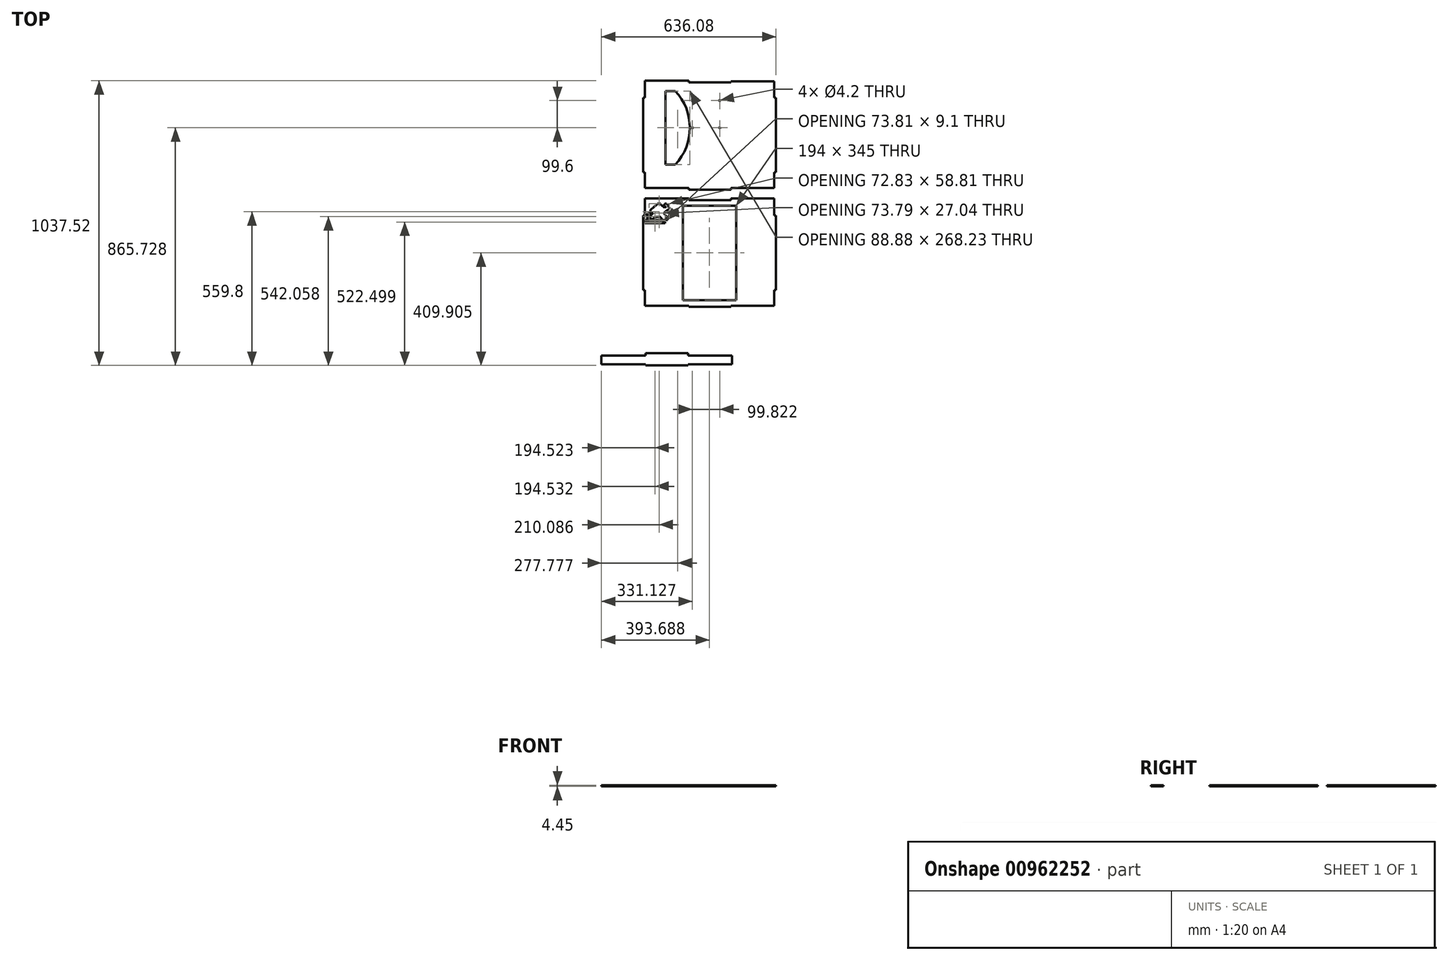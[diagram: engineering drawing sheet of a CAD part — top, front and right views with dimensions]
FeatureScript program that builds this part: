
annotation { "Feature Type Name" : "Feature", "Feature Type Description" : "" }
export const myFeature = defineFeature(function(context is Context, id is Id, definition is map)
    precondition{}
    {
        {
            var Q0;
            Q0=qCreatedBy(makeId("Top.planeOp"),FACE);
            var sketch = newSketch(context, id + "F0", { "sketchPlane" : qUnion([Q0])});
            skLineSegment(sketch, "E0.bottom", {"start": v(279.74, -310.31) * mm, "end": v(85.74, -310.31) * mm});
            skLineSegment(sketch, "E0.top", {"start": v(279.74, 34.69) * mm, "end": v(85.74, 34.69) * mm});
            skLineSegment(sketch, "E0.left", {"start": v(279.74, -310.31) * mm, "end": v(279.74, 34.69) * mm});
            skLineSegment(sketch, "E0.right", {"start": v(85.74, -310.31) * mm, "end": v(85.74, 34.69) * mm});
            skPoint(sketch, "E0.middle", {"position": v(182.74, -137.81) * mm});
            skLineSegment(sketch, "E1.bottom", {"start": v(418.8, -329.81) * mm, "end": v(260.26, -329.81) * mm});
            skLineSegment(sketch, "E1.top", {"start": v(260.26, 54.19) * mm, "end": v(107.1, 54.19) * mm});
            skLineSegment(sketch, "E1.left", {"start": v(418.8, -329.81) * mm, "end": v(418.8, -273.57) * mm});
            skLineSegment(sketch, "E1.right", {"start": v(-53.32, -329.81) * mm, "end": v(-53.32, -273.57) * mm});
            skLineSegment(sketch, "E2.top", {"start": v(-53.32, 60.52) * mm, "end": v(107.1, 60.52) * mm});
            skLineSegment(sketch, "E2.left", {"start": v(-53.32, 54.19) * mm, "end": v(-53.32, 60.52) * mm});
            skLineSegment(sketch, "E2.right", {"start": v(107.1, 54.19) * mm, "end": v(107.1, 60.52) * mm});
            skLineSegment(sketch, "E3.MirrorCS", {"start": v(260.26, 54.19) * mm, "end": v(260.26, 60.52) * mm});
            skLineSegment(sketch, "E4.top", {"start": v(107.1, -334.26) * mm, "end": v(260.26, -334.26) * mm});
            skLineSegment(sketch, "E4.left", {"start": v(107.1, -329.81) * mm, "end": v(107.1, -334.26) * mm});
            skLineSegment(sketch, "E4.right", {"start": v(260.26, -329.81) * mm, "end": v(260.26, -334.26) * mm});
            skLineSegment(sketch, "E5.trimOffspring", {"start": v(107.1, -329.81) * mm, "end": v(-53.32, -329.81) * mm});
            skLineSegment(sketch, "E6.bottom", {"start": v(425.13, -273.57) * mm, "end": v(418.8, -273.57) * mm});
            skLineSegment(sketch, "E6.top", {"start": v(425.13, -2.06) * mm, "end": v(418.8, -2.06) * mm});
            skLineSegment(sketch, "E6.left", {"start": v(425.13, -273.57) * mm, "end": v(425.13, -2.06) * mm});
            skLineSegment(sketch, "E6.right", {"start": v(-59.65, -273.57) * mm, "end": v(-59.65, -2.06) * mm});
            skLineSegment(sketch, "E7.trimOffspring", {"start": v(-53.32, -2.06) * mm, "end": v(-59.65, -2.06) * mm});
            skLineSegment(sketch, "E8.trimOffspring", {"start": v(-53.32, -273.57) * mm, "end": v(-59.65, -273.57) * mm});
            skLineSegment(sketch, "E9.trimOffspring", {"start": v(-53.32, -2.06) * mm, "end": v(-53.32, 54.19) * mm});
            skLineSegment(sketch, "E10.trimOffspring", {"start": v(418.8, -2.06) * mm, "end": v(418.8, 54.19) * mm});
            skLineSegment(sketch, "E11", {"start": v(-50.59, -20.7) * mm, "end": v(-50.59, -22.21) * mm});
            skLineSegment(sketch, "E12", {"start": v(-50.59, -22.21) * mm, "end": v(-49.15, -22.21) * mm});
            skLineSegment(sketch, "E13", {"start": v(-49.15, -22.21) * mm, "end": v(-49.15, -23.7) * mm});
            skLineSegment(sketch, "E14", {"start": v(-49.15, -23.7) * mm, "end": v(-47.72, -23.7) * mm});
            skLineSegment(sketch, "E15", {"start": v(-47.72, -23.7) * mm, "end": v(-47.72, -25.08) * mm});
            skLineSegment(sketch, "E16", {"start": v(-47.72, -25.08) * mm, "end": v(-46.45, -25.08) * mm});
            skLineSegment(sketch, "E17", {"start": v(-46.45, -25.08) * mm, "end": v(-46.45, -23.64) * mm});
            skLineSegment(sketch, "E18", {"start": v(-46.45, -23.64) * mm, "end": v(-44.99, -23.64) * mm});
            skLineSegment(sketch, "E19", {"start": v(-44.99, -23.64) * mm, "end": v(-44.99, -22.1) * mm});
            skLineSegment(sketch, "E20", {"start": v(-44.99, -22.1) * mm, "end": v(-43.53, -22.1) * mm});
            skLineSegment(sketch, "E21", {"start": v(-43.53, -22.1) * mm, "end": v(-43.53, -20.7) * mm});
            skLineSegment(sketch, "E22", {"start": v(-43.53, -20.7) * mm, "end": v(-39.25, -20.7) * mm});
            skLineSegment(sketch, "E23", {"start": v(-39.25, -20.7) * mm, "end": v(-39.25, -22.1) * mm});
            skLineSegment(sketch, "E24", {"start": v(-39.25, -22.1) * mm, "end": v(-37.82, -22.1) * mm});
            skLineSegment(sketch, "E25", {"start": v(-37.82, -22.1) * mm, "end": v(-37.82, -23.75) * mm});
            skLineSegment(sketch, "E26", {"start": v(-37.82, -23.75) * mm, "end": v(-36.36, -23.75) * mm});
            skLineSegment(sketch, "E27", {"start": v(-36.36, -23.75) * mm, "end": v(-36.36, -25.1) * mm});
            skLineSegment(sketch, "E28", {"start": v(-36.36, -25.1) * mm, "end": v(-35, -25.1) * mm});
            skLineSegment(sketch, "E29", {"start": v(-35, -25.1) * mm, "end": v(-35, -23.75) * mm});
            skLineSegment(sketch, "E30", {"start": v(-35, -23.75) * mm, "end": v(-33.6, -23.75) * mm});
            skLineSegment(sketch, "E31", {"start": v(-33.6, -23.75) * mm, "end": v(-33.6, -22.24) * mm});
            skLineSegment(sketch, "E32", {"start": v(-33.6, -22.24) * mm, "end": v(-32.2, -22.24) * mm});
            skLineSegment(sketch, "E33", {"start": v(-32.2, -22.24) * mm, "end": v(-32.2, -20.67) * mm});
            skLineSegment(sketch, "E34", {"start": v(-32.2, -20.67) * mm, "end": v(-27.9, -20.67) * mm});
            skLineSegment(sketch, "E35", {"start": v(-27.9, -20.67) * mm, "end": v(-27.9, -22.13) * mm});
            skLineSegment(sketch, "E36", {"start": v(-27.9, -22.13) * mm, "end": v(-26.46, -22.13) * mm});
            skLineSegment(sketch, "E37", {"start": v(-26.46, -22.13) * mm, "end": v(-26.46, -23.75) * mm});
            skLineSegment(sketch, "E38", {"start": v(-26.46, -23.75) * mm, "end": v(-25.03, -23.75) * mm});
            skLineSegment(sketch, "E39", {"start": v(-25.03, -23.75) * mm, "end": v(-25.03, -25.1) * mm});
            skLineSegment(sketch, "E40", {"start": v(-25.03, -25.1) * mm, "end": v(-24.14, -25.1) * mm});
            skLineSegment(sketch, "E41", {"start": v(-24.14, -25.1) * mm, "end": v(-24.14, -23.75) * mm});
            skLineSegment(sketch, "E42", {"start": v(-24.14, -23.75) * mm, "end": v(-22.98, -23.75) * mm});
            skLineSegment(sketch, "E43", {"start": v(-22.98, -23.75) * mm, "end": v(-22.98, -22.24) * mm});
            skLineSegment(sketch, "E44", {"start": v(-22.98, -22.24) * mm, "end": v(-21.62, -22.24) * mm});
            skLineSegment(sketch, "E45", {"start": v(-21.62, -22.24) * mm, "end": v(-21.62, -20.7) * mm});
            skLineSegment(sketch, "E46", {"start": v(-50.59, -20.7) * mm, "end": v(-53.32, -20.7) * mm});
            skLineSegment(sketch, "E47", {"start": v(-53.32, -20.7) * mm, "end": v(-53.32, -22.18) * mm});
            skLineSegment(sketch, "E48", {"start": v(-53.32, -22.18) * mm, "end": v(-52.02, -22.18) * mm});
            skLineSegment(sketch, "E49", {"start": v(-52.02, -22.18) * mm, "end": v(-52.02, -23.7) * mm});
            skLineSegment(sketch, "E50", {"start": v(-52.02, -23.7) * mm, "end": v(-50.59, -23.7) * mm});
            skLineSegment(sketch, "E51", {"start": v(-50.59, -23.7) * mm, "end": v(-50.59, -25.21) * mm});
            skLineSegment(sketch, "E52", {"start": v(-50.59, -25.21) * mm, "end": v(-49.18, -25.21) * mm});
            skLineSegment(sketch, "E53", {"start": v(-49.18, -25.21) * mm, "end": v(-49.18, -26.73) * mm});
            skLineSegment(sketch, "E54", {"start": v(-49.18, -26.73) * mm, "end": v(-53.32, -26.73) * mm});
            skLineSegment(sketch, "E55", {"start": v(-53.32, -26.73) * mm, "end": v(-53.32, -28.19) * mm});
            skLineSegment(sketch, "E56", {"start": v(-53.32, -28.19) * mm, "end": v(20.49, -28.19) * mm});
            skLineSegment(sketch, "E57", {"start": v(20.49, -28.19) * mm, "end": v(20.49, -25.14) * mm});
            skLineSegment(sketch, "E58", {"start": v(20.49, -25.14) * mm, "end": v(19.7, -25.14) * mm});
            skLineSegment(sketch, "E59", {"start": v(19.7, -25.14) * mm, "end": v(19.7, -23.73) * mm});
            skLineSegment(sketch, "E60", {"start": v(19.7, -23.73) * mm, "end": v(18.35, -23.73) * mm});
            skLineSegment(sketch, "E61", {"start": v(18.35, -23.73) * mm, "end": v(18.35, -22.21) * mm});
            skLineSegment(sketch, "E62", {"start": v(18.35, -22.21) * mm, "end": v(16.85, -22.21) * mm});
            skLineSegment(sketch, "E63", {"start": v(16.85, -22.21) * mm, "end": v(16.85, -20.7) * mm});
            skLineSegment(sketch, "E64", {"start": v(16.85, -20.7) * mm, "end": v(12.58, -20.7) * mm});
            skLineSegment(sketch, "E65", {"start": v(12.58, -20.7) * mm, "end": v(12.58, -22.21) * mm});
            skLineSegment(sketch, "E66", {"start": v(12.58, -22.21) * mm, "end": v(11.21, -22.21) * mm});
            skLineSegment(sketch, "E67", {"start": v(11.21, -22.21) * mm, "end": v(11.21, -23.76) * mm});
            skLineSegment(sketch, "E68", {"start": v(11.21, -23.76) * mm, "end": v(9.69, -23.76) * mm});
            skLineSegment(sketch, "E69", {"start": v(9.69, -23.76) * mm, "end": v(9.69, -25.14) * mm});
            skLineSegment(sketch, "E70.bottom", {"start": v(-21.62, -20.7) * mm, "end": v(-17.3, -20.7) * mm});
            skLineSegment(sketch, "E70.top", {"start": v(-20.12, -22.19) * mm, "end": v(-18.62, -22.19) * mm});
            skLineSegment(sketch, "E70.left", {"start": v(-21.62, -20.7) * mm, "end": v(-21.62, -22.19) * mm});
            skLineSegment(sketch, "E70.right", {"start": v(-17.3, -20.7) * mm, "end": v(-17.3, -22.19) * mm});
            skLineSegment(sketch, "E71.bottom", {"start": v(-17.3, -22.19) * mm, "end": v(-15.92, -22.19) * mm});
            skLineSegment(sketch, "E71.top", {"start": v(-18.62, -23.77) * mm, "end": v(-17.27, -23.77) * mm});
            skLineSegment(sketch, "E71.left", {"start": v(-18.62, -22.19) * mm, "end": v(-18.62, -23.77) * mm});
            skLineSegment(sketch, "E71.right", {"start": v(-15.92, -22.19) * mm, "end": v(-15.92, -23.77) * mm});
            skLineSegment(sketch, "E72.bottom", {"start": v(-15.92, -23.77) * mm, "end": v(-14.48, -23.77) * mm});
            skLineSegment(sketch, "E72.top", {"start": v(-17.27, -25.08) * mm, "end": v(-15.88, -25.08) * mm});
            skLineSegment(sketch, "E72.left", {"start": v(-17.27, -23.77) * mm, "end": v(-17.27, -25.08) * mm});
            skLineSegment(sketch, "E72.right", {"start": v(-14.48, -23.77) * mm, "end": v(-14.48, -25.08) * mm});
            skLineSegment(sketch, "E73.bottom", {"start": v(-14.48, -25.08) * mm, "end": v(-13.07, -25.08) * mm});
            skLineSegment(sketch, "E73.left", {"start": v(-15.88, -25.08) * mm, "end": v(-15.88, -26.74) * mm});
            skLineSegment(sketch, "E73.right", {"start": v(-11.62, -25.08) * mm, "end": v(-11.62, -26.74) * mm});
            skLineSegment(sketch, "E74.bottom", {"start": v(-13.07, -23.72) * mm, "end": v(-11.62, -23.72) * mm});
            skLineSegment(sketch, "E74.top", {"start": v(-11.62, -25.08) * mm, "end": v(-10.28, -25.08) * mm});
            skLineSegment(sketch, "E74.left", {"start": v(-13.07, -23.72) * mm, "end": v(-13.07, -25.08) * mm});
            skLineSegment(sketch, "E74.right", {"start": v(-10.28, -23.72) * mm, "end": v(-10.28, -25.08) * mm});
            skLineSegment(sketch, "E75.top", {"start": v(-10.28, -23.72) * mm, "end": v(-8.73, -23.72) * mm});
            skLineSegment(sketch, "E75.left", {"start": v(-11.62, -22.23) * mm, "end": v(-11.62, -23.72) * mm});
            skLineSegment(sketch, "E75.right", {"start": v(-8.73, -22.23) * mm, "end": v(-8.73, -23.72) * mm});
            skLineSegment(sketch, "E76.bottom", {"start": v(-10.26, -20.7) * mm, "end": v(-5.89, -20.7) * mm});
            skLineSegment(sketch, "E76.left", {"start": v(-10.26, -20.7) * mm, "end": v(-10.26, -22.23) * mm});
            skLineSegment(sketch, "E76.right", {"start": v(-5.89, -20.7) * mm, "end": v(-5.89, -22.23) * mm});
            skLineSegment(sketch, "E77", {"start": v(-20.12, -22.19) * mm, "end": v(-20.12, -23.66) * mm});
            skLineSegment(sketch, "E78", {"start": v(-20.12, -23.66) * mm, "end": v(-21.6, -23.66) * mm});
            skLineSegment(sketch, "E79", {"start": v(-21.6, -23.66) * mm, "end": v(-21.6, -25.18) * mm});
            skLineSegment(sketch, "E80", {"start": v(-21.6, -25.18) * mm, "end": v(-22.94, -25.18) * mm});
            skLineSegment(sketch, "E81", {"start": v(-22.94, -25.18) * mm, "end": v(-22.94, -26.67) * mm});
            skLineSegment(sketch, "E82", {"start": v(-22.94, -26.67) * mm, "end": v(-15.88, -26.74) * mm});
            skLineSegment(sketch, "E83.bottom", {"start": v(-5.89, -22.23) * mm, "end": v(-4.49, -22.23) * mm});
            skLineSegment(sketch, "E83.top", {"start": v(-7.34, -23.76) * mm, "end": v(-5.91, -23.76) * mm});
            skLineSegment(sketch, "E83.left", {"start": v(-7.34, -22.23) * mm, "end": v(-7.34, -23.76) * mm});
            skLineSegment(sketch, "E83.right", {"start": v(-4.49, -22.23) * mm, "end": v(-4.49, -23.76) * mm});
            skLineSegment(sketch, "E84.bottom", {"start": v(-4.49, -23.76) * mm, "end": v(-3.06, -23.76) * mm});
            skLineSegment(sketch, "E84.top", {"start": v(-5.91, -25.18) * mm, "end": v(-4.49, -25.18) * mm});
            skLineSegment(sketch, "E84.left", {"start": v(-5.91, -23.76) * mm, "end": v(-5.91, -25.18) * mm});
            skLineSegment(sketch, "E84.right", {"start": v(-3.06, -23.76) * mm, "end": v(-3.06, -25.18) * mm});
            skLineSegment(sketch, "E85.bottom", {"start": v(-3.06, -25.18) * mm, "end": v(-1.72, -25.18) * mm});
            skLineSegment(sketch, "E85.left", {"start": v(-4.49, -25.18) * mm, "end": v(-4.49, -26.73) * mm});
            skLineSegment(sketch, "E85.right", {"start": v(-0.26, -25.18) * mm, "end": v(-0.26, -26.73) * mm});
            skLineSegment(sketch, "E86", {"start": v(-11.62, -26.74) * mm, "end": v(-4.49, -26.73) * mm});
            skLineSegment(sketch, "E87", {"start": v(-0.26, -25.18) * mm, "end": v(1.2, -25.18) * mm});
            skLineSegment(sketch, "E88", {"start": v(1.2, -25.18) * mm, "end": v(1.2, -23.77) * mm});
            skLineSegment(sketch, "E89", {"start": v(1.2, -23.77) * mm, "end": v(2.63, -23.77) * mm});
            skLineSegment(sketch, "E90", {"start": v(2.63, -23.77) * mm, "end": v(2.63, -22.25) * mm});
            skLineSegment(sketch, "E91", {"start": v(2.63, -22.25) * mm, "end": v(3.95, -22.25) * mm});
            skLineSegment(sketch, "E92", {"start": v(3.95, -22.25) * mm, "end": v(3.95, -23.77) * mm});
            skLineSegment(sketch, "E93", {"start": v(3.95, -23.77) * mm, "end": v(5.34, -23.77) * mm});
            skLineSegment(sketch, "E94", {"start": v(5.34, -23.77) * mm, "end": v(5.34, -25.18) * mm});
            skLineSegment(sketch, "E95", {"start": v(5.34, -25.18) * mm, "end": v(6.82, -25.18) * mm});
            skLineSegment(sketch, "E96", {"start": v(6.82, -25.18) * mm, "end": v(6.82, -26.73) * mm});
            skLineSegment(sketch, "E97", {"start": v(6.82, -26.73) * mm, "end": v(-0.26, -26.73) * mm});
            skLineSegment(sketch, "E98.right", {"start": v(11.18, -25.18) * mm, "end": v(11.18, -26.73) * mm});
            skLineSegment(sketch, "E99", {"start": v(11.18, -25.18) * mm, "end": v(12.64, -25.18) * mm});
            skLineSegment(sketch, "E100", {"start": v(12.64, -25.18) * mm, "end": v(12.64, -23.77) * mm});
            skLineSegment(sketch, "E101", {"start": v(12.64, -23.77) * mm, "end": v(14.07, -23.77) * mm});
            skLineSegment(sketch, "E102", {"start": v(14.07, -23.77) * mm, "end": v(14.07, -22.25) * mm});
            skLineSegment(sketch, "E103", {"start": v(14.07, -22.25) * mm, "end": v(15.4, -22.25) * mm});
            skLineSegment(sketch, "E104", {"start": v(15.4, -22.25) * mm, "end": v(15.4, -23.77) * mm});
            skLineSegment(sketch, "E105", {"start": v(15.4, -23.77) * mm, "end": v(16.79, -23.77) * mm});
            skLineSegment(sketch, "E106", {"start": v(16.79, -23.77) * mm, "end": v(16.79, -25.18) * mm});
            skLineSegment(sketch, "E107", {"start": v(16.79, -25.18) * mm, "end": v(18.26, -25.18) * mm});
            skLineSegment(sketch, "E108", {"start": v(18.26, -25.18) * mm, "end": v(18.26, -26.73) * mm});
            skLineSegment(sketch, "E109", {"start": v(18.26, -26.73) * mm, "end": v(11.18, -26.73) * mm});
            skLineSegment(sketch, "E110", {"start": v(-1.72, -25.18) * mm, "end": v(-1.72, -23.84) * mm});
            skLineSegment(sketch, "E111", {"start": v(-1.72, -23.84) * mm, "end": v(-1.72, -23.76) * mm});
            skLineSegment(sketch, "E112", {"start": v(-1.72, -23.76) * mm, "end": v(-0.3, -23.76) * mm});
            skLineSegment(sketch, "E113", {"start": v(-0.3, -23.76) * mm, "end": v(-0.3, -22.23) * mm});
            skLineSegment(sketch, "E114", {"start": v(-0.3, -22.23) * mm, "end": v(1.15, -22.23) * mm});
            skLineSegment(sketch, "E115", {"start": v(1.15, -22.23) * mm, "end": v(1.15, -20.69) * mm});
            skLineSegment(sketch, "E116", {"start": v(1.15, -20.69) * mm, "end": v(5.42, -20.69) * mm});
            skLineSegment(sketch, "E117", {"start": v(5.42, -20.69) * mm, "end": v(5.42, -22.13) * mm});
            skLineSegment(sketch, "E118", {"start": v(5.42, -22.13) * mm, "end": v(6.87, -22.13) * mm});
            skLineSegment(sketch, "E119", {"start": v(6.87, -22.13) * mm, "end": v(6.87, -23.76) * mm});
            skLineSegment(sketch, "E120", {"start": v(6.87, -23.76) * mm, "end": v(8.33, -23.76) * mm});
            skLineSegment(sketch, "E121", {"start": v(8.33, -23.76) * mm, "end": v(8.33, -25.14) * mm});
            skLineSegment(sketch, "E122", {"start": v(8.33, -25.14) * mm, "end": v(9.69, -25.14) * mm});
            skLineSegment(sketch, "E123", {"start": v(-8.73, -22.23) * mm, "end": v(-7.34, -22.23) * mm});
            skLineSegment(sketch, "E124.top", {"start": v(-30.79, -22.25) * mm, "end": v(-29.29, -22.25) * mm});
            skLineSegment(sketch, "E125.top", {"start": v(-29.29, -23.83) * mm, "end": v(-27.94, -23.83) * mm});
            skLineSegment(sketch, "E125.left", {"start": v(-29.29, -22.25) * mm, "end": v(-29.29, -23.83) * mm});
            skLineSegment(sketch, "E126.top", {"start": v(-27.94, -25.14) * mm, "end": v(-26.54, -25.14) * mm});
            skLineSegment(sketch, "E126.left", {"start": v(-27.94, -23.83) * mm, "end": v(-27.94, -25.14) * mm});
            skLineSegment(sketch, "E127.left", {"start": v(-26.54, -25.14) * mm, "end": v(-26.54, -26.8) * mm});
            skLineSegment(sketch, "E128", {"start": v(-30.79, -22.25) * mm, "end": v(-30.79, -23.72) * mm});
            skLineSegment(sketch, "E129", {"start": v(-30.79, -23.72) * mm, "end": v(-32.18, -23.72) * mm});
            skLineSegment(sketch, "E130", {"start": v(-32.18, -23.72) * mm, "end": v(-32.18, -25.2) * mm});
            skLineSegment(sketch, "E131", {"start": v(-32.18, -25.2) * mm, "end": v(-33.6, -25.2) * mm});
            skLineSegment(sketch, "E132", {"start": v(-33.6, -26.73) * mm, "end": v(-26.54, -26.8) * mm});
            skLineSegment(sketch, "E133", {"start": v(-33.6, -25.2) * mm, "end": v(-33.6, -26.73) * mm});
            skLineSegment(sketch, "E134.top", {"start": v(-42.05, -22.22) * mm, "end": v(-40.64, -22.22) * mm});
            skLineSegment(sketch, "E135.top", {"start": v(-40.64, -23.78) * mm, "end": v(-39.26, -23.78) * mm});
            skLineSegment(sketch, "E135.left", {"start": v(-40.64, -22.22) * mm, "end": v(-40.64, -23.78) * mm});
            skLineSegment(sketch, "E136.top", {"start": v(-39.26, -25.2) * mm, "end": v(-37.8, -25.2) * mm});
            skLineSegment(sketch, "E136.left", {"start": v(-39.26, -23.78) * mm, "end": v(-39.26, -25.2) * mm});
            skLineSegment(sketch, "E137.left", {"start": v(-37.8, -25.2) * mm, "end": v(-37.8, -26.77) * mm});
            skLineSegment(sketch, "E138", {"start": v(-42.05, -22.22) * mm, "end": v(-42.05, -23.78) * mm});
            skLineSegment(sketch, "E139", {"start": v(-42.05, -23.78) * mm, "end": v(-43.45, -23.78) * mm});
            skLineSegment(sketch, "E140", {"start": v(-43.45, -23.78) * mm, "end": v(-43.45, -25.16) * mm});
            skLineSegment(sketch, "E141", {"start": v(-43.45, -25.16) * mm, "end": v(-44.86, -25.16) * mm});
            skLineSegment(sketch, "E142", {"start": v(-44.86, -26.7) * mm, "end": v(-37.8, -26.77) * mm});
            skLineSegment(sketch, "E143", {"start": v(-44.86, -25.16) * mm, "end": v(-44.86, -26.7) * mm});
            skLineSegment(sketch, "E144", {"start": v(-53.32, -19.18) * mm, "end": v(20.47, -19.18) * mm});
            skLineSegment(sketch, "E145", {"start": v(20.47, -19.18) * mm, "end": v(20.47, -20.7) * mm});
            skLineSegment(sketch, "E146", {"start": v(20.47, -20.7) * mm, "end": v(-53.32, -20.7) * mm});
            skLineSegment(sketch, "E147", {"start": v(20.47, -19.18) * mm, "end": v(20.47, -17.87) * mm});
            skLineSegment(sketch, "E148", {"start": v(20.47, -17.87) * mm, "end": v(-53.32, -17.87) * mm});
            skLineSegment(sketch, "E149", {"start": v(-53.32, -17.87) * mm, "end": v(-53.32, -19.18) * mm});
            skLineSegment(sketch, "E150", {"start": v(20.49, -28.19) * mm, "end": v(20.49, -29.77) * mm});
            skLineSegment(sketch, "E151", {"start": v(20.49, -29.77) * mm, "end": v(-53.32, -29.77) * mm});
            skLineSegment(sketch, "E152", {"start": v(-53.32, -29.77) * mm, "end": v(-53.32, -28.19) * mm});
            skLineSegment(sketch, "E153", {"start": v(-43.76, -17.87) * mm, "end": v(-43.76, 4.94) * mm});
            skLineSegment(sketch, "E154", {"start": v(-43.76, 4.94) * mm, "end": v(-42.35, 4.94) * mm});
            skLineSegment(sketch, "E155", {"start": v(-42.35, 4.94) * mm, "end": v(-42.35, 6.3) * mm});
            skLineSegment(sketch, "E156", {"start": v(-42.35, 6.3) * mm, "end": v(-40.93, 6.3) * mm});
            skLineSegment(sketch, "E157", {"start": v(-40.93, 6.3) * mm, "end": v(-40.93, 7.86) * mm});
            skLineSegment(sketch, "E158", {"start": v(-40.93, 7.86) * mm, "end": v(-35.2, 7.86) * mm});
            skLineSegment(sketch, "E159", {"start": v(-35.2, 7.86) * mm, "end": v(-35.2, 4.83) * mm});
            skLineSegment(sketch, "E160", {"start": v(-35.2, 4.83) * mm, "end": v(-36.59, 4.83) * mm});
            skLineSegment(sketch, "E161", {"start": v(-36.59, 4.83) * mm, "end": v(-36.59, 3.59) * mm});
            skLineSegment(sketch, "E162", {"start": v(-36.59, 3.59) * mm, "end": v(-38.02, 3.59) * mm});
            skLineSegment(sketch, "E163", {"start": v(-38.02, 3.59) * mm, "end": v(-38.02, 1.92) * mm});
            skLineSegment(sketch, "E164", {"start": v(-38.02, 1.92) * mm, "end": v(-42.22, 1.92) * mm});
            skLineSegment(sketch, "E165", {"start": v(-42.22, 1.92) * mm, "end": v(-42.22, -14.87) * mm});
            skLineSegment(sketch, "E166", {"start": v(-42.22, -14.87) * mm, "end": v(-40.93, -14.87) * mm});
            skLineSegment(sketch, "E167", {"start": v(-40.93, -14.87) * mm, "end": v(-40.93, -16.35) * mm});
            skLineSegment(sketch, "E168", {"start": v(-40.93, -16.35) * mm, "end": v(-39.58, -16.35) * mm});
            skLineSegment(sketch, "E169", {"start": v(-39.58, -16.35) * mm, "end": v(-39.58, -17.87) * mm});
            skLineSegment(sketch, "E170", {"start": v(-37.2, -13.65) * mm, "end": v(-19.84, -13.65) * mm});
            skLineSegment(sketch, "E171", {"start": v(-19.84, -13.65) * mm, "end": v(-19.84, -10.02) * mm});
            skLineSegment(sketch, "E172", {"start": v(-19.84, -10.02) * mm, "end": v(-18.11, -10.02) * mm});
            skLineSegment(sketch, "E173", {"start": v(-18.11, -10.02) * mm, "end": v(-18.11, -8.18) * mm});
            skLineSegment(sketch, "E174", {"start": v(-18.11, -8.18) * mm, "end": v(-11.79, -8.18) * mm});
            skLineSegment(sketch, "E175", {"start": v(-11.79, -8.18) * mm, "end": v(-11.79, -6.34) * mm});
            skLineSegment(sketch, "E176", {"start": v(-11.79, -6.34) * mm, "end": v(3.84, -6.34) * mm});
            skLineSegment(sketch, "E177", {"start": v(3.84, -6.34) * mm, "end": v(3.84, -8.12) * mm});
            skLineSegment(sketch, "E178", {"start": v(3.84, -8.12) * mm, "end": v(5.41, -8.12) * mm});
            skLineSegment(sketch, "E179", {"start": v(5.41, -8.12) * mm, "end": v(5.41, -10.13) * mm});
            skLineSegment(sketch, "E180", {"start": v(5.41, -10.13) * mm, "end": v(7.04, -10.13) * mm});
            skLineSegment(sketch, "E181", {"start": v(7.04, -10.13) * mm, "end": v(7.04, -11.91) * mm});
            skLineSegment(sketch, "E182", {"start": v(7.04, -11.91) * mm, "end": v(8.6, -11.91) * mm});
            skLineSegment(sketch, "E183", {"start": v(8.6, -11.91) * mm, "end": v(8.6, -15.48) * mm});
            skLineSegment(sketch, "E184", {"start": v(8.6, -15.48) * mm, "end": v(10.23, -15.48) * mm});
            skLineSegment(sketch, "E185", {"start": v(10.23, -15.48) * mm, "end": v(10.23, -17.32) * mm});
            skLineSegment(sketch, "E186", {"start": v(10.23, -17.32) * mm, "end": v(29.26, -17.32) * mm});
            skLineSegment(sketch, "E187", {"start": v(29.26, -17.32) * mm, "end": v(29.26, -15.54) * mm});
            skLineSegment(sketch, "E188", {"start": v(29.26, -15.54) * mm, "end": v(27.75, -15.54) * mm});
            skLineSegment(sketch, "E189", {"start": v(27.75, -15.54) * mm, "end": v(27.75, -13.54) * mm});
            skLineSegment(sketch, "E190", {"start": v(27.75, -13.54) * mm, "end": v(26.13, -13.54) * mm});
            skLineSegment(sketch, "E191", {"start": v(26.13, -13.54) * mm, "end": v(26.13, -11.8) * mm});
            skLineSegment(sketch, "E192", {"start": v(26.13, -11.8) * mm, "end": v(23, -11.8) * mm});
            skLineSegment(sketch, "E193", {"start": v(23, -11.8) * mm, "end": v(23, -8.24) * mm});
            skLineSegment(sketch, "E194", {"start": v(23, -8.24) * mm, "end": v(24.67, -8.24) * mm});
            skLineSegment(sketch, "E195", {"start": v(24.67, -8.24) * mm, "end": v(24.67, -2.56) * mm});
            skLineSegment(sketch, "E196", {"start": v(24.67, -2.56) * mm, "end": v(22.83, -2.56) * mm});
            skLineSegment(sketch, "E197", {"start": v(22.83, -2.56) * mm, "end": v(22.83, -0.72) * mm});
            skLineSegment(sketch, "E198", {"start": v(22.83, -0.72) * mm, "end": v(21.26, -0.72) * mm});
            skLineSegment(sketch, "E199", {"start": v(21.26, -0.72) * mm, "end": v(21.26, 1.08) * mm});
            skLineSegment(sketch, "E200", {"start": v(21.26, 1.08) * mm, "end": v(19.74, 1.08) * mm});
            skLineSegment(sketch, "E201", {"start": v(19.74, 1.08) * mm, "end": v(19.74, 3.07) * mm});
            skLineSegment(sketch, "E202", {"start": v(19.74, 3.07) * mm, "end": v(18.23, 3.07) * mm});
            skLineSegment(sketch, "E203", {"start": v(18.23, 3.07) * mm, "end": v(18.23, 10.04) * mm});
            skLineSegment(sketch, "E204", {"start": v(18.23, 10.04) * mm, "end": v(19.74, 10.04) * mm});
            skLineSegment(sketch, "E205", {"start": v(19.74, 10.04) * mm, "end": v(19.74, 11.88) * mm});
            skLineSegment(sketch, "E206", {"start": v(19.74, 11.88) * mm, "end": v(21.48, 11.88) * mm});
            skLineSegment(sketch, "E207", {"start": v(21.48, 11.88) * mm, "end": v(21.48, 13.88) * mm});
            skLineSegment(sketch, "E208", {"start": v(21.48, 13.88) * mm, "end": v(24.77, 13.88) * mm});
            skLineSegment(sketch, "E209", {"start": v(24.77, 13.88) * mm, "end": v(24.77, 15.72) * mm});
            skLineSegment(sketch, "E210", {"start": v(24.77, 15.72) * mm, "end": v(27.73, 15.72) * mm});
            skLineSegment(sketch, "E211", {"start": v(27.73, 15.72) * mm, "end": v(27.73, 17.57) * mm});
            skLineSegment(sketch, "E212", {"start": v(27.73, 17.57) * mm, "end": v(29.25, 17.57) * mm});
            skLineSegment(sketch, "E213", {"start": v(29.25, 17.57) * mm, "end": v(29.25, 19.2) * mm});
            skLineSegment(sketch, "E214", {"start": v(29.25, 19.2) * mm, "end": v(32.32, 19.2) * mm});
            skLineSegment(sketch, "E215", {"start": v(32.32, 19.2) * mm, "end": v(32.32, 21.18) * mm});
            skLineSegment(sketch, "E216", {"start": v(32.32, 21.18) * mm, "end": v(33.84, 21.18) * mm});
            skLineSegment(sketch, "E217", {"start": v(33.84, 21.18) * mm, "end": v(33.84, 23) * mm});
            skLineSegment(sketch, "E218", {"start": v(33.84, 23) * mm, "end": v(35.55, 23) * mm});
            skLineSegment(sketch, "E219", {"start": v(35.55, 23) * mm, "end": v(35.55, 28.62) * mm});
            skLineSegment(sketch, "E220", {"start": v(35.55, 28.62) * mm, "end": v(33.84, 28.62) * mm});
            skLineSegment(sketch, "E221", {"start": v(33.84, 28.62) * mm, "end": v(33.84, 34.25) * mm});
            skLineSegment(sketch, "E222", {"start": v(33.84, 34.25) * mm, "end": v(32.44, 34.25) * mm});
            skLineSegment(sketch, "E223", {"start": v(32.44, 34.25) * mm, "end": v(32.44, 37.87) * mm});
            skLineSegment(sketch, "E224", {"start": v(32.44, 37.87) * mm, "end": v(29.25, 37.87) * mm});
            skLineSegment(sketch, "E225", {"start": v(29.25, 37.87) * mm, "end": v(29.25, 39.7) * mm});
            skLineSegment(sketch, "E226", {"start": v(29.25, 39.7) * mm, "end": v(26.03, 39.7) * mm});
            skLineSegment(sketch, "E227", {"start": v(26.03, 39.7) * mm, "end": v(26.03, 41.48) * mm});
            skLineSegment(sketch, "E228", {"start": v(26.03, 41.48) * mm, "end": v(19.66, 41.48) * mm});
            skLineSegment(sketch, "E229", {"start": v(19.66, 41.48) * mm, "end": v(19.66, 39.7) * mm});
            skLineSegment(sketch, "E230", {"start": v(19.66, 39.7) * mm, "end": v(18.23, 39.7) * mm});
            skLineSegment(sketch, "E231", {"start": v(18.23, 39.7) * mm, "end": v(18.23, 37.96) * mm});
            skLineSegment(sketch, "E232", {"start": v(18.23, 37.96) * mm, "end": v(16.58, 37.96) * mm});
            skLineSegment(sketch, "E233", {"start": v(16.58, 37.96) * mm, "end": v(16.58, 35.98) * mm});
            skLineSegment(sketch, "E234", {"start": v(16.58, 35.98) * mm, "end": v(18.08, 35.98) * mm});
            skLineSegment(sketch, "E235", {"start": v(18.08, 35.98) * mm, "end": v(18.08, 32.35) * mm});
            skLineSegment(sketch, "E236", {"start": v(18.08, 32.35) * mm, "end": v(19.63, 32.35) * mm});
            skLineSegment(sketch, "E237", {"start": v(19.63, 32.35) * mm, "end": v(19.63, 30.46) * mm});
            skLineSegment(sketch, "E238", {"start": v(19.63, 30.46) * mm, "end": v(24.42, 30.46) * mm});
            skLineSegment(sketch, "E239", {"start": v(24.42, 30.46) * mm, "end": v(24.42, 28.65) * mm});
            skLineSegment(sketch, "E240", {"start": v(24.42, 28.65) * mm, "end": v(15, 28.65) * mm});
            skLineSegment(sketch, "E241", {"start": v(15, 28.65) * mm, "end": v(15, 30.52) * mm});
            skLineSegment(sketch, "E242", {"start": v(15, 30.52) * mm, "end": v(13.62, 30.52) * mm});
            skLineSegment(sketch, "E243", {"start": v(13.62, 30.52) * mm, "end": v(13.62, 32.35) * mm});
            skLineSegment(sketch, "E244", {"start": v(13.62, 32.35) * mm, "end": v(11.86, 32.35) * mm});
            skLineSegment(sketch, "E245", {"start": v(11.86, 32.35) * mm, "end": v(11.86, 34.15) * mm});
            skLineSegment(sketch, "E246", {"start": v(11.86, 34.15) * mm, "end": v(8.73, 34.15) * mm});
            skLineSegment(sketch, "E247", {"start": v(8.73, 34.15) * mm, "end": v(8.73, 36) * mm});
            skLineSegment(sketch, "E248", {"start": v(8.73, 36) * mm, "end": v(7.07, 36) * mm});
            skLineSegment(sketch, "E249", {"start": v(7.07, 36) * mm, "end": v(7.07, 37.85) * mm});
            skLineSegment(sketch, "E250", {"start": v(7.07, 37.85) * mm, "end": v(5.6, 37.85) * mm});
            skLineSegment(sketch, "E251", {"start": v(5.6, 37.85) * mm, "end": v(5.6, 39.82) * mm});
            skLineSegment(sketch, "E252", {"start": v(5.6, 39.82) * mm, "end": v(4.03, 39.82) * mm});
            skLineSegment(sketch, "E253", {"start": v(4.03, 39.82) * mm, "end": v(4.03, 41.45) * mm});
            skLineSegment(sketch, "E254", {"start": v(4.03, 41.45) * mm, "end": v(-7, 41.45) * mm});
            skLineSegment(sketch, "E255", {"start": v(-7, 41.45) * mm, "end": v(-7, 39.77) * mm});
            skLineSegment(sketch, "E256", {"start": v(-7, 39.77) * mm, "end": v(-8.65, 39.77) * mm});
            skLineSegment(sketch, "E257", {"start": v(-8.65, 39.77) * mm, "end": v(-8.65, 37.85) * mm});
            skLineSegment(sketch, "E258", {"start": v(-8.65, 37.85) * mm, "end": v(-10.14, 37.85) * mm});
            skLineSegment(sketch, "E259", {"start": v(-10.14, 37.85) * mm, "end": v(-10.14, 36.17) * mm});
            skLineSegment(sketch, "E260", {"start": v(-10.14, 36.17) * mm, "end": v(-11.84, 36.17) * mm});
            skLineSegment(sketch, "E261", {"start": v(-11.84, 36.17) * mm, "end": v(-11.84, 34.25) * mm});
            skLineSegment(sketch, "E262", {"start": v(-11.84, 34.25) * mm, "end": v(-16.68, 34.25) * mm});
            skLineSegment(sketch, "E263", {"start": v(-16.68, 34.25) * mm, "end": v(-16.68, 32.35) * mm});
            skLineSegment(sketch, "E264", {"start": v(-16.68, 32.35) * mm, "end": v(-18.2, 32.35) * mm});
            skLineSegment(sketch, "E265", {"start": v(-18.2, 32.35) * mm, "end": v(-18.2, 28.76) * mm});
            skLineSegment(sketch, "E266", {"start": v(-18.2, 28.76) * mm, "end": v(-21.3, 28.76) * mm});
            skLineSegment(sketch, "E267", {"start": v(-21.3, 28.76) * mm, "end": v(-21.3, 26.83) * mm});
            skLineSegment(sketch, "E268", {"start": v(-21.3, 26.83) * mm, "end": v(-24.55, 26.83) * mm});
            skLineSegment(sketch, "E269", {"start": v(-24.55, 26.83) * mm, "end": v(-24.55, 24.98) * mm});
            skLineSegment(sketch, "E270", {"start": v(-24.55, 24.98) * mm, "end": v(-26.2, 24.98) * mm});
            skLineSegment(sketch, "E271", {"start": v(-26.2, 24.98) * mm, "end": v(-26.2, 23.23) * mm});
            skLineSegment(sketch, "E272", {"start": v(-26.2, 23.23) * mm, "end": v(-29.34, 23.23) * mm});
            skLineSegment(sketch, "E273", {"start": v(-29.34, 23.23) * mm, "end": v(-29.34, 21.33) * mm});
            skLineSegment(sketch, "E274", {"start": v(-29.34, 21.33) * mm, "end": v(-30.94, 21.33) * mm});
            skLineSegment(sketch, "E275", {"start": v(-30.94, 21.33) * mm, "end": v(-30.94, 19.45) * mm});
            skLineSegment(sketch, "E276", {"start": v(-30.94, 19.45) * mm, "end": v(-32.55, 19.45) * mm});
            skLineSegment(sketch, "E277", {"start": v(-32.55, 19.45) * mm, "end": v(-32.55, 12.07) * mm});
            skLineSegment(sketch, "E278", {"start": v(-32.55, 12.07) * mm, "end": v(-30.78, 12.07) * mm});
            skLineSegment(sketch, "E279", {"start": v(-30.78, 12.07) * mm, "end": v(-30.78, 10.16) * mm});
            skLineSegment(sketch, "E280", {"start": v(-30.78, 10.16) * mm, "end": v(-29.34, 10.16) * mm});
            skLineSegment(sketch, "E281", {"start": v(-29.34, 10.16) * mm, "end": v(-29.34, 8.44) * mm});
            skLineSegment(sketch, "E282", {"start": v(-29.34, 8.44) * mm, "end": v(-27.66, 8.44) * mm});
            skLineSegment(sketch, "E283", {"start": v(-27.66, 8.44) * mm, "end": v(-27.66, 6.45) * mm});
            skLineSegment(sketch, "E284", {"start": v(-27.66, 6.45) * mm, "end": v(-22.77, 6.45) * mm});
            skLineSegment(sketch, "E285", {"start": v(-22.77, 6.45) * mm, "end": v(-22.77, 4.73) * mm});
            skLineSegment(sketch, "E286", {"start": v(-22.77, 4.73) * mm, "end": v(-26.25, 4.73) * mm});
            skLineSegment(sketch, "E287", {"start": v(-26.25, 4.73) * mm, "end": v(-26.25, 3) * mm});
            skLineSegment(sketch, "E288", {"start": v(-26.25, 3) * mm, "end": v(-29.3, 3) * mm});
            skLineSegment(sketch, "E289", {"start": v(-29.3, 3) * mm, "end": v(-29.3, 1.13) * mm});
            skLineSegment(sketch, "E290", {"start": v(-29.3, 1.13) * mm, "end": v(-30.87, 1.13) * mm});
            skLineSegment(sketch, "E291", {"start": v(-30.87, 1.13) * mm, "end": v(-30.87, -6.29) * mm});
            skLineSegment(sketch, "E292", {"start": v(-30.87, -6.29) * mm, "end": v(-32.55, -6.29) * mm});
            skLineSegment(sketch, "E293", {"start": v(-32.55, -6.29) * mm, "end": v(-32.55, -8.12) * mm});
            skLineSegment(sketch, "E294", {"start": v(-32.55, -8.12) * mm, "end": v(-35.67, -8.12) * mm});
            skLineSegment(sketch, "E295", {"start": v(-35.67, -8.12) * mm, "end": v(-35.67, -10.05) * mm});
            skLineSegment(sketch, "E296", {"start": v(-35.67, -10.05) * mm, "end": v(-37.28, -10.05) * mm});
            skLineSegment(sketch, "E297", {"start": v(-37.28, -10.05) * mm, "end": v(-37.2, -13.65) * mm});
            skLineSegment(sketch, "E298.bottom", {"start": v(12, 12.16) * mm, "end": v(10.1, 12.16) * mm});
            skLineSegment(sketch, "E298.top", {"start": v(12, 10.22) * mm, "end": v(10.1, 10.22) * mm});
            skLineSegment(sketch, "E298.left", {"start": v(12, 12.16) * mm, "end": v(12, 10.22) * mm});
            skLineSegment(sketch, "E298.right", {"start": v(10.1, 12.16) * mm, "end": v(10.1, 10.22) * mm});
            skLineSegment(sketch, "E299.bottom", {"start": v(12, 10.22) * mm, "end": v(13.45, 10.22) * mm});
            skLineSegment(sketch, "E299.top", {"start": v(12, 8.43) * mm, "end": v(13.45, 8.43) * mm});
            skLineSegment(sketch, "E299.left", {"start": v(12, 10.22) * mm, "end": v(12, 8.43) * mm});
            skLineSegment(sketch, "E299.right", {"start": v(13.45, 10.22) * mm, "end": v(13.45, 8.43) * mm});
            skLineSegment(sketch, "E300.bottom", {"start": v(12, 8.43) * mm, "end": v(8.65, 8.43) * mm});
            skLineSegment(sketch, "E300.top", {"start": v(12, 4.86) * mm, "end": v(8.65, 4.86) * mm});
            skLineSegment(sketch, "E300.left", {"start": v(12, 8.43) * mm, "end": v(12, 4.86) * mm});
            skLineSegment(sketch, "E300.right", {"start": v(8.65, 8.43) * mm, "end": v(8.65, 4.86) * mm});
            skLineSegment(sketch, "E301.bottom", {"start": v(10.33, 4.86) * mm, "end": v(8.65, 4.86) * mm});
            skLineSegment(sketch, "E301.top", {"start": v(10.33, 2.86) * mm, "end": v(8.65, 2.86) * mm});
            skLineSegment(sketch, "E301.left", {"start": v(10.33, 4.86) * mm, "end": v(10.33, 2.86) * mm});
            skLineSegment(sketch, "E301.right", {"start": v(8.65, 4.86) * mm, "end": v(8.65, 2.86) * mm});
            skLineSegment(sketch, "E302.bottom", {"start": v(10.33, 2.86) * mm, "end": v(12, 2.86) * mm});
            skLineSegment(sketch, "E302.top", {"start": v(10.33, 1.02) * mm, "end": v(12, 1.02) * mm});
            skLineSegment(sketch, "E302.left", {"start": v(10.33, 2.86) * mm, "end": v(10.33, 1.02) * mm});
            skLineSegment(sketch, "E302.right", {"start": v(12, 2.86) * mm, "end": v(12, 1.02) * mm});
            skLineSegment(sketch, "E303.bottom", {"start": v(12, 2.86) * mm, "end": v(13.57, 2.86) * mm});
            skLineSegment(sketch, "E303.top", {"start": v(12, 4.75) * mm, "end": v(13.57, 4.75) * mm});
            skLineSegment(sketch, "E303.left", {"start": v(12, 2.86) * mm, "end": v(12, 4.75) * mm});
            skLineSegment(sketch, "E303.right", {"start": v(13.57, 2.86) * mm, "end": v(13.57, 4.75) * mm});
            skLineSegment(sketch, "E304.bottom", {"start": v(8.65, 8.43) * mm, "end": v(7.05, 8.43) * mm});
            skLineSegment(sketch, "E304.top", {"start": v(7.05, 10.24) * mm, "end": v(7.05, 10.24) * mm});
            skLineSegment(sketch, "E304.left", {"start": v(8.65, 8.43) * mm, "end": v(8.65, 10.24) * mm});
            skLineSegment(sketch, "E304.right", {"start": v(7.05, 8.43) * mm, "end": v(7.05, 10.24) * mm});
            skLineSegment(sketch, "E305.top", {"start": v(8.65, 12.06) * mm, "end": v(7.05, 12.06) * mm});
            skLineSegment(sketch, "E305.left", {"start": v(8.65, 10.24) * mm, "end": v(8.65, 12.06) * mm});
            skLineSegment(sketch, "E306.bottom", {"start": v(7.05, 12.06) * mm, "end": v(5.54, 12.06) * mm});
            skLineSegment(sketch, "E306.top", {"start": v(7.05, 10.24) * mm, "end": v(5.54, 10.24) * mm});
            skLineSegment(sketch, "E307.bottom", {"start": v(5.54, 12.06) * mm, "end": v(3.92, 12.06) * mm});
            skLineSegment(sketch, "E307.top", {"start": v(5.54, 10.24) * mm, "end": v(3.92, 10.24) * mm});
            skLineSegment(sketch, "E308.bottom", {"start": v(3.92, 12.06) * mm, "end": v(2.4, 12.06) * mm});
            skLineSegment(sketch, "E308.top", {"start": v(3.92, 10.24) * mm, "end": v(2.4, 10.24) * mm});
            skLineSegment(sketch, "E309.bottom", {"start": v(2.4, 12.06) * mm, "end": v(0.75, 12.06) * mm});
            skLineSegment(sketch, "E309.top", {"start": v(2.4, 10.24) * mm, "end": v(0.75, 10.24) * mm});
            skLineSegment(sketch, "E310.bottom", {"start": v(0.75, 12.06) * mm, "end": v(-0.73, 12.06) * mm});
            skLineSegment(sketch, "E310.top", {"start": v(0.75, 10.24) * mm, "end": v(-0.73, 10.24) * mm});
            skLineSegment(sketch, "E310.right", {"start": v(-0.73, 12.06) * mm, "end": v(-0.73, 10.24) * mm});
            skLineSegment(sketch, "E311", {"start": v(8.65, 2.86) * mm, "end": v(0.8, 2.86) * mm});
            skLineSegment(sketch, "E312", {"start": v(0.8, 2.86) * mm, "end": v(0.8, 4.76) * mm});
            skLineSegment(sketch, "E313", {"start": v(0.8, 4.76) * mm, "end": v(-0.72, 4.76) * mm});
            skLineSegment(sketch, "E314", {"start": v(-0.72, 4.76) * mm, "end": v(-0.73, 10.24) * mm});
            skLineSegment(sketch, "E315", {"start": v(0.8, 2.86) * mm, "end": v(-0.73, 2.86) * mm});
            skLineSegment(sketch, "E316", {"start": v(-0.73, 2.86) * mm, "end": v(-0.72, 4.76) * mm});
            skLineSegment(sketch, "E317", {"start": v(-0.72, 4.76) * mm, "end": v(-4.02, 4.78) * mm});
            skLineSegment(sketch, "E318", {"start": v(-4.02, 4.78) * mm, "end": v(-4.02, 10.24) * mm});
            skLineSegment(sketch, "E319", {"start": v(-4.02, 10.24) * mm, "end": v(-0.73, 10.24) * mm});
            skLineSegment(sketch, "E320", {"start": v(-4.02, 10.24) * mm, "end": v(-4.02, 12.09) * mm});
            skLineSegment(sketch, "E321", {"start": v(-4.02, 12.09) * mm, "end": v(-8.66, 12.09) * mm});
            skLineSegment(sketch, "E322", {"start": v(-8.66, 12.09) * mm, "end": v(-8.66, 14.02) * mm});
            skLineSegment(sketch, "E323", {"start": v(-8.66, 14.02) * mm, "end": v(-13.6, 14.02) * mm});
            skLineSegment(sketch, "E324", {"start": v(-13.6, 14.02) * mm, "end": v(-13.6, 10.24) * mm});
            skLineSegment(sketch, "E325", {"start": v(-13.6, 10.24) * mm, "end": v(-11.88, 10.24) * mm});
            skLineSegment(sketch, "E326", {"start": v(-11.88, 10.24) * mm, "end": v(-11.88, 8.4) * mm});
            skLineSegment(sketch, "E327", {"start": v(-11.88, 8.4) * mm, "end": v(-8.69, 8.4) * mm});
            skLineSegment(sketch, "E328", {"start": v(-8.69, 10.24) * mm, "end": v(-8.69, 8.4) * mm});
            skLineSegment(sketch, "E329", {"start": v(-10.2, 6.55) * mm, "end": v(-11.8, 6.53) * mm});
            skLineSegment(sketch, "E330", {"start": v(-11.8, 6.53) * mm, "end": v(-11.88, 8.4) * mm});
            skLineSegment(sketch, "E331", {"start": v(-8.72, 6.54) * mm, "end": v(-8.68, 4.72) * mm});
            skLineSegment(sketch, "E332", {"start": v(-8.68, 4.72) * mm, "end": v(-10.2, 4.7) * mm});
            skLineSegment(sketch, "E333", {"start": v(-10.2, 4.7) * mm, "end": v(-10.2, 6.55) * mm});
            skLineSegment(sketch, "E334", {"start": v(-8.72, 6.54) * mm, "end": v(-10.2, 6.54) * mm});
            skLineSegment(sketch, "E335", {"start": v(-10.3, 8.4) * mm, "end": v(-10.3, 6.55) * mm});
            skPoint(sketch, "E336.start.orphan", {"position": v(-8.45, 10.24) * mm});
            skLineSegment(sketch, "E337", {"start": v(-8.69, 10.24) * mm, "end": v(-10.27, 10.24) * mm});
            skLineSegment(sketch, "E338", {"start": v(-10.27, 10.24) * mm, "end": v(-10.3, 8.4) * mm});
            skLineSegment(sketch, "E339", {"start": v(-11.8, 6.53) * mm, "end": v(-11.78, 4.88) * mm});
            skLineSegment(sketch, "E340", {"start": v(-11.78, 4.88) * mm, "end": v(-16.64, 4.88) * mm});
            skLineSegment(sketch, "E341", {"start": v(-16.64, 4.88) * mm, "end": v(-16.64, 2.9) * mm});
            skLineSegment(sketch, "E342", {"start": v(-16.64, 2.9) * mm, "end": v(-13.54, 2.9) * mm});
            skLineSegment(sketch, "E343", {"start": v(-13.54, 2.9) * mm, "end": v(-13.54, 0.97) * mm});
            skLineSegment(sketch, "E344", {"start": v(-13.54, 0.97) * mm, "end": v(-11.8, 0.97) * mm});
            skLineSegment(sketch, "E345", {"start": v(-11.8, 0.97) * mm, "end": v(-11.8, -2.59) * mm});
            skLineSegment(sketch, "E346", {"start": v(-11.8, -2.59) * mm, "end": v(-10.26, -2.59) * mm});
            skLineSegment(sketch, "E347", {"start": v(-10.26, -2.59) * mm, "end": v(-10.26, -4.63) * mm});
            skLineSegment(sketch, "E348", {"start": v(-10.26, -4.63) * mm, "end": v(-11.8, -4.63) * mm});
            skLineSegment(sketch, "E349", {"start": v(-11.8, -4.63) * mm, "end": v(-11.79, -6.34) * mm});
            skPoint(sketch, "E350.oppositeSnap0", {"position": v(0.04, 2.86) * mm});
            skLineSegment(sketch, "E350.bottom", {"start": v(-4.02, 4.78) * mm, "end": v(-5.51, 4.78) * mm});
            skLineSegment(sketch, "E350.top", {"start": v(-4.02, 2.86) * mm, "end": v(-5.51, 2.86) * mm});
            skLineSegment(sketch, "E350.left", {"start": v(-4.02, 4.78) * mm, "end": v(-4.02, 2.86) * mm});
            skLineSegment(sketch, "E350.right", {"start": v(-5.51, 4.78) * mm, "end": v(-5.51, 2.86) * mm});
            skLineSegment(sketch, "E351.bottom", {"start": v(-5.51, 2.93) * mm, "end": v(-13.54, 2.93) * mm});
            skLineSegment(sketch, "E351.top", {"start": v(-5.51, 0.97) * mm, "end": v(-13.54, 0.97) * mm});
            skLineSegment(sketch, "E351.left", {"start": v(-5.51, 2.93) * mm, "end": v(-5.51, 0.97) * mm});
            skLineSegment(sketch, "E351.right", {"start": v(-13.54, 2.93) * mm, "end": v(-13.54, 0.97) * mm});
            skLineSegment(sketch, "E352.bottom", {"start": v(-11.8, 0.97) * mm, "end": v(-10.26, 0.97) * mm});
            skLineSegment(sketch, "E352.right", {"start": v(-10.26, 0.97) * mm, "end": v(-10.26, -2.59) * mm});
            skLineSegment(sketch, "E353.bottom", {"start": v(-10.26, -2.59) * mm, "end": v(-8.68, -2.59) * mm});
            skLineSegment(sketch, "E353.top", {"start": v(-10.26, -4.6) * mm, "end": v(-8.68, -4.6) * mm});
            skLineSegment(sketch, "E353.left", {"start": v(-10.26, -2.59) * mm, "end": v(-10.26, -4.6) * mm});
            skLineSegment(sketch, "E353.right", {"start": v(-8.68, -2.59) * mm, "end": v(-8.68, -4.6) * mm});
            skLineSegment(sketch, "E354.bottom", {"start": v(-8.68, -2.59) * mm, "end": v(-7.04, -2.59) * mm});
            skLineSegment(sketch, "E354.top", {"start": v(-8.68, -0.82) * mm, "end": v(-7.04, -0.82) * mm});
            skLineSegment(sketch, "E354.left", {"start": v(-8.68, -2.59) * mm, "end": v(-8.68, -0.82) * mm});
            skLineSegment(sketch, "E354.right", {"start": v(-7.04, -2.59) * mm, "end": v(-7.04, -0.82) * mm});
            skLineSegment(sketch, "E355.bottom", {"start": v(-7.04, -2.59) * mm, "end": v(-5.55, -2.59) * mm});
            skLineSegment(sketch, "E355.top", {"start": v(-7.04, -6.34) * mm, "end": v(-5.55, -6.34) * mm});
            skLineSegment(sketch, "E355.left", {"start": v(-7.04, -2.59) * mm, "end": v(-7.04, -6.34) * mm});
            skLineSegment(sketch, "E355.right", {"start": v(-5.55, -2.59) * mm, "end": v(-5.55, -6.34) * mm});
            skLineSegment(sketch, "E356.bottom", {"start": v(-10.26, -6.34) * mm, "end": v(-7.04, -6.34) * mm});
            skLineSegment(sketch, "E356.top", {"start": v(-10.26, -4.6) * mm, "end": v(-7.04, -4.6) * mm});
            skLineSegment(sketch, "E356.left", {"start": v(-10.26, -6.34) * mm, "end": v(-10.26, -4.6) * mm});
            skLineSegment(sketch, "E356.right", {"start": v(-7.04, -6.34) * mm, "end": v(-7.04, -4.6) * mm});
            skLineSegment(sketch, "E357.bottom", {"start": v(-5.55, -4.6) * mm, "end": v(-3.97, -4.6) * mm});
            skLineSegment(sketch, "E357.top", {"start": v(-5.55, -6.34) * mm, "end": v(-3.97, -6.34) * mm});
            skLineSegment(sketch, "E357.left", {"start": v(-5.55, -4.6) * mm, "end": v(-5.55, -6.34) * mm});
            skLineSegment(sketch, "E357.right", {"start": v(-3.97, -4.6) * mm, "end": v(-3.97, -6.34) * mm});
            skLineSegment(sketch, "E358.bottom", {"start": v(-3.97, -4.6) * mm, "end": v(-5.55, -4.6) * mm});
            skLineSegment(sketch, "E358.top", {"start": v(-3.97, -2.59) * mm, "end": v(-5.55, -2.59) * mm});
            skLineSegment(sketch, "E358.left", {"start": v(-3.97, -4.6) * mm, "end": v(-3.97, -2.59) * mm});
            skLineSegment(sketch, "E358.right", {"start": v(-5.55, -4.6) * mm, "end": v(-5.55, -2.59) * mm});
            skLineSegment(sketch, "E359.bottom", {"start": v(-5.55, -2.59) * mm, "end": v(-3.97, -2.59) * mm});
            skLineSegment(sketch, "E359.top", {"start": v(-5.55, -0.85) * mm, "end": v(-3.97, -0.85) * mm});
            skLineSegment(sketch, "E359.left", {"start": v(-5.55, -2.59) * mm, "end": v(-5.55, -0.85) * mm});
            skLineSegment(sketch, "E359.right", {"start": v(-3.97, -2.59) * mm, "end": v(-3.97, -0.85) * mm});
            skLineSegment(sketch, "E360.bottom", {"start": v(-3.97, -2.59) * mm, "end": v(-2.37, -2.59) * mm});
            skLineSegment(sketch, "E360.top", {"start": v(-3.97, -6.34) * mm, "end": v(-2.37, -6.34) * mm});
            skLineSegment(sketch, "E360.left", {"start": v(-3.97, -2.59) * mm, "end": v(-3.97, -6.34) * mm});
            skLineSegment(sketch, "E360.right", {"start": v(-2.37, -2.59) * mm, "end": v(-2.37, -6.34) * mm});
            skLineSegment(sketch, "E361.bottom", {"start": v(0.7, -6.34) * mm, "end": v(-0.8, -6.34) * mm});
            skLineSegment(sketch, "E361.top", {"start": v(0.7, -2.59) * mm, "end": v(-0.8, -2.59) * mm});
            skLineSegment(sketch, "E361.left", {"start": v(0.7, -6.34) * mm, "end": v(0.7, -2.59) * mm});
            skLineSegment(sketch, "E361.right", {"start": v(-0.8, -6.34) * mm, "end": v(-0.8, -2.59) * mm});
            skLineSegment(sketch, "E362.bottom", {"start": v(-0.8, -4.47) * mm, "end": v(-2.37, -4.47) * mm});
            skLineSegment(sketch, "E362.top", {"start": v(-0.8, -6.34) * mm, "end": v(-2.37, -6.34) * mm});
            skLineSegment(sketch, "E362.left", {"start": v(-0.8, -4.47) * mm, "end": v(-0.8, -6.34) * mm});
            skLineSegment(sketch, "E362.right", {"start": v(-2.37, -4.47) * mm, "end": v(-2.37, -6.34) * mm});
            skLineSegment(sketch, "E363.bottom", {"start": v(-0.8, -2.59) * mm, "end": v(0.7, -2.59) * mm});
            skLineSegment(sketch, "E363.top", {"start": v(-0.8, -0.8) * mm, "end": v(0.7, -0.8) * mm});
            skLineSegment(sketch, "E363.left", {"start": v(-0.8, -2.59) * mm, "end": v(-0.8, -0.8) * mm});
            skLineSegment(sketch, "E363.right", {"start": v(0.7, -2.59) * mm, "end": v(0.7, -0.8) * mm});
            skLineSegment(sketch, "E364.bottom", {"start": v(0.7, -6.34) * mm, "end": v(2.35, -6.34) * mm});
            skLineSegment(sketch, "E364.top", {"start": v(0.7, -2.59) * mm, "end": v(2.35, -2.59) * mm});
            skLineSegment(sketch, "E364.right", {"start": v(2.35, -6.34) * mm, "end": v(2.35, -2.59) * mm});
            skLineSegment(sketch, "E365.bottom", {"start": v(2.35, -2.59) * mm, "end": v(3.92, -2.59) * mm});
            skLineSegment(sketch, "E365.top", {"start": v(2.35, -0.81) * mm, "end": v(3.92, -0.81) * mm});
            skLineSegment(sketch, "E365.left", {"start": v(2.35, -2.59) * mm, "end": v(2.35, -0.81) * mm});
            skLineSegment(sketch, "E365.right", {"start": v(3.92, -2.59) * mm, "end": v(3.92, -0.81) * mm});
            skLineSegment(sketch, "E366.bottom", {"start": v(3.92, -2.59) * mm, "end": v(5.59, -2.59) * mm});
            skLineSegment(sketch, "E366.top", {"start": v(3.92, -4.6) * mm, "end": v(5.59, -4.6) * mm});
            skLineSegment(sketch, "E366.left", {"start": v(3.92, -2.59) * mm, "end": v(3.92, -4.6) * mm});
            skLineSegment(sketch, "E366.right", {"start": v(5.59, -2.59) * mm, "end": v(5.59, -4.6) * mm});
            skLineSegment(sketch, "E367.bottom", {"start": v(3.92, -4.6) * mm, "end": v(2.35, -4.6) * mm});
            skLineSegment(sketch, "E367.top", {"start": v(3.92, -2.59) * mm, "end": v(2.35, -2.59) * mm});
            skLineSegment(sketch, "E367.left", {"start": v(3.92, -4.6) * mm, "end": v(3.92, -2.59) * mm});
            skLineSegment(sketch, "E367.right", {"start": v(2.35, -4.6) * mm, "end": v(2.35, -2.59) * mm});
            skLineSegment(sketch, "E368.bottom", {"start": v(8.65, 2.86) * mm, "end": v(0.7, 2.86) * mm});
            skLineSegment(sketch, "E368.top", {"start": v(8.65, 0.97) * mm, "end": v(0.7, 0.97) * mm});
            skLineSegment(sketch, "E368.left", {"start": v(8.65, 2.86) * mm, "end": v(8.65, 0.97) * mm});
            skLineSegment(sketch, "E368.right", {"start": v(0.7, 2.86) * mm, "end": v(0.7, 0.97) * mm});
            skLineSegment(sketch, "E369.bottom", {"start": v(7.14, 0.97) * mm, "end": v(5.59, 0.97) * mm});
            skLineSegment(sketch, "E369.top", {"start": v(7.14, -2.59) * mm, "end": v(5.59, -2.59) * mm});
            skLineSegment(sketch, "E369.left", {"start": v(7.14, 0.97) * mm, "end": v(7.14, -2.59) * mm});
            skLineSegment(sketch, "E369.right", {"start": v(5.59, 0.97) * mm, "end": v(5.59, -2.59) * mm});
            skLineSegment(sketch, "E370.bottom", {"start": v(5.59, -4.6) * mm, "end": v(6.96, -4.6) * mm});
            skLineSegment(sketch, "E370.top", {"start": v(5.59, -6.34) * mm, "end": v(6.96, -6.34) * mm});
            skLineSegment(sketch, "E370.left", {"start": v(5.59, -4.6) * mm, "end": v(5.59, -6.34) * mm});
            skLineSegment(sketch, "E370.right", {"start": v(6.96, -4.6) * mm, "end": v(6.96, -6.34) * mm});
            skLineSegment(sketch, "E371.bottom", {"start": v(-15.04, 14.02) * mm, "end": v(-16.58, 14.02) * mm});
            skLineSegment(sketch, "E371.top", {"start": v(-15.04, 12.01) * mm, "end": v(-19.83, 12.01) * mm});
            skLineSegment(sketch, "E371.left", {"start": v(-15.04, 14.02) * mm, "end": v(-15.04, 12.01) * mm});
            skLineSegment(sketch, "E371.right", {"start": v(-19.83, 14.02) * mm, "end": v(-19.83, 12.01) * mm});
            skLineSegment(sketch, "E372.bottom", {"start": v(-16.58, 15.8) * mm, "end": v(-19.83, 15.8) * mm});
            skLineSegment(sketch, "E372.top", {"start": v(-19.83, 14.02) * mm, "end": v(-21.3, 14.02) * mm});
            skLineSegment(sketch, "E372.left", {"start": v(-16.58, 15.8) * mm, "end": v(-16.58, 14.02) * mm});
            skLineSegment(sketch, "E372.right", {"start": v(-21.3, 15.8) * mm, "end": v(-21.3, 14.02) * mm});
            skLineSegment(sketch, "E373.bottom", {"start": v(-19.83, 17.61) * mm, "end": v(-22.98, 17.61) * mm});
            skLineSegment(sketch, "E373.top", {"start": v(-21.3, 15.8) * mm, "end": v(-22.98, 15.8) * mm});
            skLineSegment(sketch, "E373.left", {"start": v(-19.83, 17.61) * mm, "end": v(-19.83, 15.8) * mm});
            skLineSegment(sketch, "E373.right", {"start": v(-22.98, 17.61) * mm, "end": v(-22.98, 15.8) * mm});
            skLineSegment(sketch, "E374.bottom", {"start": v(-22.98, 17.61) * mm, "end": v(-24.56, 17.61) * mm});
            skLineSegment(sketch, "E374.top", {"start": v(-22.98, 19.42) * mm, "end": v(-24.56, 19.42) * mm});
            skLineSegment(sketch, "E374.left", {"start": v(-22.98, 17.61) * mm, "end": v(-22.98, 19.42) * mm});
            skLineSegment(sketch, "E374.right", {"start": v(-24.56, 17.61) * mm, "end": v(-24.56, 19.42) * mm});
            skLineSegment(sketch, "E375", {"start": v(-4.02, 10.24) * mm, "end": v(-5.5, 10.24) * mm});
            skLineSegment(sketch, "E376", {"start": v(-5.5, 10.24) * mm, "end": v(-5.5, 12.09) * mm});
            skLineSegment(sketch, "E377", {"start": v(5.57, 6.56) * mm, "end": v(5.57, 4.73) * mm});
            skLineSegment(sketch, "E378", {"start": v(5.57, 4.73) * mm, "end": v(3.96, 4.73) * mm});
            skLineSegment(sketch, "E379", {"start": v(3.96, 4.73) * mm, "end": v(3.96, 6.53) * mm});
            skLineSegment(sketch, "E380", {"start": v(3.96, 6.53) * mm, "end": v(5.57, 6.56) * mm});
            skPoint(sketch, "E381.oppositeSnap0", {"position": v(26.13, -12.67) * mm});
            skLineSegment(sketch, "E381.bottom", {"start": v(27.75, -15.54) * mm, "end": v(26.13, -15.54) * mm});
            skLineSegment(sketch, "E381.top", {"start": v(27.75, -17.32) * mm, "end": v(26.13, -17.32) * mm});
            skLineSegment(sketch, "E381.left", {"start": v(27.75, -15.54) * mm, "end": v(27.75, -17.32) * mm});
            skLineSegment(sketch, "E381.right", {"start": v(26.13, -15.54) * mm, "end": v(26.13, -17.32) * mm});
            skLineSegment(sketch, "E382.bottom", {"start": v(26.13, -15.54) * mm, "end": v(24.58, -15.54) * mm});
            skLineSegment(sketch, "E382.top", {"start": v(26.13, -13.84) * mm, "end": v(24.58, -13.84) * mm});
            skLineSegment(sketch, "E382.left", {"start": v(26.13, -15.54) * mm, "end": v(26.13, -13.84) * mm});
            skLineSegment(sketch, "E382.right", {"start": v(24.58, -15.54) * mm, "end": v(24.58, -13.84) * mm});
            skLineSegment(sketch, "E383.bottom", {"start": v(24.58, -13.84) * mm, "end": v(23, -13.84) * mm});
            skLineSegment(sketch, "E383.top", {"start": v(24.58, -11.8) * mm, "end": v(23, -11.8) * mm});
            skLineSegment(sketch, "E383.left", {"start": v(24.58, -13.84) * mm, "end": v(24.58, -11.8) * mm});
            skLineSegment(sketch, "E383.right", {"start": v(23, -13.84) * mm, "end": v(23, -11.8) * mm});
            skLineSegment(sketch, "E384.bottom", {"start": v(21.37, -13.84) * mm, "end": v(19.68, -13.84) * mm});
            skLineSegment(sketch, "E384.top", {"start": v(21.37, -15.54) * mm, "end": v(19.68, -15.54) * mm});
            skLineSegment(sketch, "E384.left", {"start": v(21.37, -13.84) * mm, "end": v(21.37, -15.54) * mm});
            skLineSegment(sketch, "E384.right", {"start": v(19.68, -13.84) * mm, "end": v(19.68, -15.54) * mm});
            skLineSegment(sketch, "E385.bottom", {"start": v(19.68, -11.8) * mm, "end": v(14.98, -11.8) * mm});
            skLineSegment(sketch, "E385.top", {"start": v(19.68, -13.84) * mm, "end": v(14.98, -13.84) * mm});
            skLineSegment(sketch, "E385.left", {"start": v(19.68, -11.8) * mm, "end": v(19.68, -13.84) * mm});
            skLineSegment(sketch, "E385.right", {"start": v(14.98, -11.8) * mm, "end": v(14.98, -13.84) * mm});
            skLineSegment(sketch, "E386.bottom", {"start": v(11.8, -11.8) * mm, "end": v(10.28, -11.8) * mm});
            skLineSegment(sketch, "E386.top", {"start": v(11.8, -13.84) * mm, "end": v(10.28, -13.84) * mm});
            skLineSegment(sketch, "E386.left", {"start": v(11.8, -11.8) * mm, "end": v(11.8, -13.84) * mm});
            skLineSegment(sketch, "E386.right", {"start": v(10.28, -11.8) * mm, "end": v(10.28, -13.84) * mm});
            skLineSegment(sketch, "E387.bottom", {"start": v(11.8, -13.84) * mm, "end": v(13.49, -13.84) * mm});
            skLineSegment(sketch, "E387.top", {"start": v(11.8, -15.54) * mm, "end": v(13.49, -15.54) * mm});
            skLineSegment(sketch, "E387.left", {"start": v(11.8, -13.84) * mm, "end": v(11.8, -15.54) * mm});
            skLineSegment(sketch, "E387.right", {"start": v(13.49, -13.84) * mm, "end": v(13.49, -15.54) * mm});
            skLineSegment(sketch, "E388", {"start": v(23, -8.24) * mm, "end": v(22.83, -2.56) * mm});
            skLineSegment(sketch, "E389", {"start": v(22.83, -2.56) * mm, "end": v(21.33, -2.6) * mm});
            skLineSegment(sketch, "E390", {"start": v(21.33, -2.6) * mm, "end": v(21.26, -0.72) * mm});
            skLineSegment(sketch, "E391", {"start": v(21.26, -0.72) * mm, "end": v(19.77, -0.77) * mm});
            skLineSegment(sketch, "E392", {"start": v(19.77, -0.77) * mm, "end": v(19.74, 1.08) * mm});
            skLineSegment(sketch, "E393", {"start": v(18.27, 1.08) * mm, "end": v(19.76, 1.08) * mm});
            skLineSegment(sketch, "E394", {"start": v(18.27, 1.08) * mm, "end": v(18.23, 3.07) * mm});
            skLineSegment(sketch, "E395.bottom", {"start": v(18.23, 4.79) * mm, "end": v(16.62, 4.79) * mm});
            skLineSegment(sketch, "E395.top", {"start": v(18.23, 2.91) * mm, "end": v(16.62, 2.91) * mm});
            skLineSegment(sketch, "E395.left", {"start": v(18.23, 4.79) * mm, "end": v(18.23, 2.91) * mm});
            skLineSegment(sketch, "E395.right", {"start": v(16.62, 4.79) * mm, "end": v(16.62, 2.91) * mm});
            skLineSegment(sketch, "E396.bottom", {"start": v(-15.15, -0.74) * mm, "end": v(-16.56, -0.74) * mm});
            skLineSegment(sketch, "E396.top", {"start": v(-15.15, -2.74) * mm, "end": v(-16.56, -2.74) * mm});
            skLineSegment(sketch, "E396.left", {"start": v(-15.15, -0.74) * mm, "end": v(-15.15, -2.74) * mm});
            skLineSegment(sketch, "E396.right", {"start": v(-16.56, -0.74) * mm, "end": v(-16.56, -2.74) * mm});
            skLineSegment(sketch, "E397.bottom", {"start": v(-19.83, 4.76) * mm, "end": v(-26.25, 4.76) * mm});
            skLineSegment(sketch, "E397.top", {"start": v(-19.83, 3) * mm, "end": v(-26.25, 3) * mm});
            skLineSegment(sketch, "E397.left", {"start": v(-19.83, 4.76) * mm, "end": v(-19.83, 3) * mm});
            skLineSegment(sketch, "E397.right", {"start": v(-26.25, 4.76) * mm, "end": v(-26.25, 3) * mm});
            skLineSegment(sketch, "E398.top", {"start": v(-26.25, 1.13) * mm, "end": v(-29.3, 1.13) * mm});
            skLineSegment(sketch, "E398.left", {"start": v(-26.25, 3) * mm, "end": v(-26.25, 1.13) * mm});
            skLineSegment(sketch, "E399.top", {"start": v(-29.3, -2.58) * mm, "end": v(-30.87, -2.58) * mm});
            skLineSegment(sketch, "E399.left", {"start": v(-29.3, 1.13) * mm, "end": v(-29.3, -2.58) * mm});
            skLineSegment(sketch, "E399.right", {"start": v(-30.87, 1.13) * mm, "end": v(-30.87, -2.58) * mm});
            skLineSegment(sketch, "E400.bottom", {"start": v(29.18, 25.1) * mm, "end": v(27.73, 25.1) * mm});
            skLineSegment(sketch, "E400.top", {"start": v(29.18, 23.2) * mm, "end": v(27.73, 23.2) * mm});
            skLineSegment(sketch, "E400.left", {"start": v(29.18, 25.1) * mm, "end": v(29.18, 23.2) * mm});
            skLineSegment(sketch, "E400.right", {"start": v(27.73, 25.1) * mm, "end": v(27.73, 23.2) * mm});
            skLineSegment(sketch, "E401.bottom", {"start": v(27.82, 30.65) * mm, "end": v(24.36, 30.65) * mm});
            skLineSegment(sketch, "E401.top", {"start": v(26.11, 26.56) * mm, "end": v(24.36, 26.56) * mm});
            skLineSegment(sketch, "E401.left", {"start": v(27.82, 30.65) * mm, "end": v(27.82, 26.56) * mm});
            skLineSegment(sketch, "E401.right", {"start": v(24.36, 30.65) * mm, "end": v(24.36, 26.56) * mm});
            skLineSegment(sketch, "E402.top", {"start": v(27.82, 25) * mm, "end": v(26.11, 25) * mm});
            skLineSegment(sketch, "E402.left", {"start": v(27.82, 26.56) * mm, "end": v(27.82, 25) * mm});
            skLineSegment(sketch, "E402.right", {"start": v(26.11, 26.56) * mm, "end": v(26.11, 25) * mm});
            skLineSegment(sketch, "E403", {"start": v(-19.75, 28.76) * mm, "end": v(-19.75, 26.86) * mm});
            skLineSegment(sketch, "E404", {"start": v(-19.75, 26.86) * mm, "end": v(-21.3, 26.83) * mm});
            skLineSegment(sketch, "E405.bottom", {"start": v(-24.55, 26.83) * mm, "end": v(-21.28, 26.83) * mm});
            skLineSegment(sketch, "E405.top", {"start": v(-24.55, 24.9) * mm, "end": v(-21.28, 24.9) * mm});
            skLineSegment(sketch, "E405.left", {"start": v(-24.55, 26.83) * mm, "end": v(-24.55, 24.9) * mm});
            skLineSegment(sketch, "E405.right", {"start": v(-21.28, 26.83) * mm, "end": v(-21.28, 24.9) * mm});
            skLineSegment(sketch, "E406.bottom", {"start": v(-26.2, 24.98) * mm, "end": v(-24.55, 24.98) * mm});
            skLineSegment(sketch, "E406.top", {"start": v(-26.2, 23.2) * mm, "end": v(-24.55, 23.2) * mm});
            skLineSegment(sketch, "E406.left", {"start": v(-26.2, 24.98) * mm, "end": v(-26.2, 23.2) * mm});
            skLineSegment(sketch, "E406.right", {"start": v(-24.55, 24.98) * mm, "end": v(-24.55, 23.2) * mm});
            skLineSegment(sketch, "E407.bottom", {"start": v(-29.34, 23.23) * mm, "end": v(-26.2, 23.23) * mm});
            skLineSegment(sketch, "E407.top", {"start": v(-29.34, 21.31) * mm, "end": v(-26.2, 21.31) * mm});
            skLineSegment(sketch, "E407.left", {"start": v(-29.34, 23.23) * mm, "end": v(-29.34, 21.31) * mm});
            skLineSegment(sketch, "E407.right", {"start": v(-26.2, 23.23) * mm, "end": v(-26.2, 21.31) * mm});
            skLineSegment(sketch, "E408.bottom", {"start": v(-30.94, 21.33) * mm, "end": v(-29.34, 21.33) * mm});
            skLineSegment(sketch, "E408.top", {"start": v(-30.94, 19.45) * mm, "end": v(-29.34, 19.45) * mm});
            skLineSegment(sketch, "E408.right", {"start": v(-29.34, 21.33) * mm, "end": v(-29.34, 19.45) * mm});
            skLineSegment(sketch, "E409.bottom", {"start": v(30.8, 34.28) * mm, "end": v(29.17, 34.28) * mm});
            skLineSegment(sketch, "E409.top", {"start": v(30.8, 30.5) * mm, "end": v(29.17, 30.5) * mm});
            skLineSegment(sketch, "E409.left", {"start": v(30.8, 34.28) * mm, "end": v(30.8, 30.5) * mm});
            skLineSegment(sketch, "E409.right", {"start": v(29.17, 34.28) * mm, "end": v(29.17, 30.5) * mm});
            skLineSegment(sketch, "E410.bottom", {"start": v(29.17, 32.38) * mm, "end": v(27.82, 32.38) * mm});
            skLineSegment(sketch, "E410.top", {"start": v(29.17, 30.44) * mm, "end": v(27.82, 30.44) * mm});
            skLineSegment(sketch, "E410.left", {"start": v(29.17, 32.38) * mm, "end": v(29.17, 30.44) * mm});
            skLineSegment(sketch, "E410.right", {"start": v(27.82, 32.38) * mm, "end": v(27.82, 30.44) * mm});
            skLineSegment(sketch, "E411.bottom", {"start": v(27.82, 37.98) * mm, "end": v(26.06, 37.98) * mm});
            skLineSegment(sketch, "E411.top", {"start": v(27.82, 36.09) * mm, "end": v(26.06, 36.09) * mm});
            skLineSegment(sketch, "E411.left", {"start": v(27.82, 37.98) * mm, "end": v(27.82, 36.09) * mm});
            skLineSegment(sketch, "E411.right", {"start": v(26.06, 37.98) * mm, "end": v(26.06, 36.09) * mm});
            skLineSegment(sketch, "E412.bottom", {"start": v(26.06, 36.09) * mm, "end": v(24.52, 36.09) * mm});
            skLineSegment(sketch, "E412.top", {"start": v(26.06, 34.22) * mm, "end": v(24.52, 34.22) * mm});
            skLineSegment(sketch, "E412.left", {"start": v(26.06, 36.09) * mm, "end": v(26.06, 34.22) * mm});
            skLineSegment(sketch, "E412.right", {"start": v(24.52, 36.09) * mm, "end": v(24.52, 34.22) * mm});
            skLineSegment(sketch, "E413.bottom", {"start": v(24.52, 34.22) * mm, "end": v(22.98, 34.22) * mm});
            skLineSegment(sketch, "E413.top", {"start": v(24.52, 32.3) * mm, "end": v(22.98, 32.3) * mm});
            skLineSegment(sketch, "E413.left", {"start": v(24.52, 34.22) * mm, "end": v(24.52, 32.3) * mm});
            skLineSegment(sketch, "E413.right", {"start": v(22.98, 34.22) * mm, "end": v(22.98, 32.3) * mm});
            skLineSegment(sketch, "E414.bottom", {"start": v(22.98, 34.22) * mm, "end": v(18.08, 34.22) * mm});
            skLineSegment(sketch, "E414.top", {"start": v(22.98, 35.98) * mm, "end": v(18.08, 35.98) * mm});
            skLineSegment(sketch, "E414.left", {"start": v(22.98, 34.22) * mm, "end": v(22.98, 35.98) * mm});
            skLineSegment(sketch, "E414.right", {"start": v(18.08, 34.22) * mm, "end": v(18.08, 35.98) * mm});
            skLineSegment(sketch, "E415.bottom", {"start": v(21.36, 35.98) * mm, "end": v(19.68, 35.98) * mm});
            skLineSegment(sketch, "E415.top", {"start": v(21.36, 37.9) * mm, "end": v(19.68, 37.9) * mm});
            skLineSegment(sketch, "E415.left", {"start": v(21.36, 35.98) * mm, "end": v(21.36, 37.9) * mm});
            skLineSegment(sketch, "E415.right", {"start": v(19.68, 35.98) * mm, "end": v(19.68, 37.9) * mm});
            skLineSegment(sketch, "E416.bottom", {"start": v(21.36, 37.9) * mm, "end": v(22.98, 37.9) * mm});
            skLineSegment(sketch, "E416.top", {"start": v(21.36, 39.69) * mm, "end": v(22.98, 39.69) * mm});
            skLineSegment(sketch, "E416.left", {"start": v(21.36, 37.9) * mm, "end": v(21.36, 39.69) * mm});
            skLineSegment(sketch, "E416.right", {"start": v(22.98, 37.9) * mm, "end": v(22.98, 39.69) * mm});
            skLineSegment(sketch, "E417", {"start": v(13.62, 30.52) * mm, "end": v(13.62, 28.75) * mm});
            skLineSegment(sketch, "E418", {"start": v(13.62, 28.75) * mm, "end": v(10.31, 28.75) * mm});
            skLineSegment(sketch, "E419", {"start": v(10.31, 28.75) * mm, "end": v(10.31, 26.82) * mm});
            skLineSegment(sketch, "E420", {"start": v(10.31, 26.82) * mm, "end": v(11.99, 26.82) * mm});
            skLineSegment(sketch, "E421", {"start": v(11.99, 26.82) * mm, "end": v(11.99, 21.26) * mm});
            skLineSegment(sketch, "E422", {"start": v(11.99, 21.26) * mm, "end": v(10.18, 21.26) * mm});
            skLineSegment(sketch, "E423", {"start": v(10.18, 21.26) * mm, "end": v(10.18, 19.36) * mm});
            skLineSegment(sketch, "E424", {"start": v(10.18, 19.36) * mm, "end": v(8.64, 19.36) * mm});
            skLineSegment(sketch, "E425", {"start": v(8.64, 19.36) * mm, "end": v(8.64, 17.69) * mm});
            skLineSegment(sketch, "E426", {"start": v(8.64, 17.69) * mm, "end": v(5.49, 17.69) * mm});
            skLineSegment(sketch, "E427", {"start": v(5.49, 17.69) * mm, "end": v(5.49, 15.98) * mm});
            skLineSegment(sketch, "E428", {"start": v(5.49, 15.98) * mm, "end": v(-8.66, 15.98) * mm});
            skLineSegment(sketch, "E429", {"start": v(-8.66, 15.98) * mm, "end": v(-8.66, 17.53) * mm});
            skLineSegment(sketch, "E430", {"start": v(-8.66, 17.53) * mm, "end": v(-13.61, 17.53) * mm});
            skLineSegment(sketch, "E431", {"start": v(-13.61, 17.53) * mm, "end": v(-13.61, 19.42) * mm});
            skLineSegment(sketch, "E432", {"start": v(-13.61, 19.42) * mm, "end": v(-15.16, 19.42) * mm});
            skLineSegment(sketch, "E433", {"start": v(-15.16, 19.42) * mm, "end": v(-15.16, 21.39) * mm});
            skLineSegment(sketch, "E434", {"start": v(-15.16, 21.39) * mm, "end": v(-16.76, 21.39) * mm});
            skLineSegment(sketch, "E435", {"start": v(-16.76, 21.39) * mm, "end": v(-16.76, 26.85) * mm});
            skLineSegment(sketch, "E436", {"start": v(-16.76, 26.85) * mm, "end": v(-15.12, 26.85) * mm});
            skLineSegment(sketch, "E437", {"start": v(-15.12, 26.85) * mm, "end": v(-15.12, 28.6) * mm});
            skLineSegment(sketch, "E438", {"start": v(-15.12, 28.6) * mm, "end": v(-18.2, 28.6) * mm});
            skLineSegment(sketch, "E439", {"start": v(-18.2, 28.6) * mm, "end": v(-18.2, 28.76) * mm});
            skLineSegment(sketch, "E440", {"start": v(0.75, 12.06) * mm, "end": v(0.75, 10.24) * mm});
            skLineSegment(sketch, "E441", {"start": v(2.4, 12.06) * mm, "end": v(2.4, 10.24) * mm});
            skLineSegment(sketch, "E442", {"start": v(7.05, 12.06) * mm, "end": v(7.05, 10.24) * mm});
            skLineSegment(sketch, "E443", {"start": v(8.65, 10.24) * mm, "end": v(7.05, 10.24) * mm});
            skLineSegment(sketch, "E444", {"start": v(5.54, 12.06) * mm, "end": v(5.54, 10.24) * mm});
            skLineSegment(sketch, "E445", {"start": v(3.92, 12.06) * mm, "end": v(3.92, 10.24) * mm});
            skLineSegment(sketch, "E446", {"start": v(-32.55, -8.12) * mm, "end": v(-30.84, -8.12) * mm});
            skLineSegment(sketch, "E447", {"start": v(-30.84, -8.12) * mm, "end": v(-30.84, -10.04) * mm});
            skLineSegment(sketch, "E448", {"start": v(-30.84, -10.04) * mm, "end": v(-32.55, -10.04) * mm});
            skLineSegment(sketch, "E449", {"start": v(-32.55, -10.04) * mm, "end": v(-32.55, -11.76) * mm});
            skLineSegment(sketch, "E450", {"start": v(-32.55, -11.76) * mm, "end": v(-30.99, -11.76) * mm});
            skLineSegment(sketch, "E451", {"start": v(-30.99, -11.76) * mm, "end": v(-30.99, -10.04) * mm});
            skLineSegment(sketch, "E452", {"start": v(-30.99, -10.04) * mm, "end": v(-30.84, -10.04) * mm});
            skLineSegment(sketch, "E453.bottom", {"start": v(-27.88, -13.65) * mm, "end": v(-26.2, -13.65) * mm});
            skLineSegment(sketch, "E453.top", {"start": v(-27.88, -11.83) * mm, "end": v(-26.2, -11.83) * mm});
            skLineSegment(sketch, "E453.left", {"start": v(-27.88, -13.65) * mm, "end": v(-27.88, -11.83) * mm});
            skLineSegment(sketch, "E453.right", {"start": v(-26.2, -13.65) * mm, "end": v(-26.2, -11.83) * mm});
            skLineSegment(sketch, "E454.bottom", {"start": v(-5.6, 34.26) * mm, "end": v(-2.42, 34.26) * mm});
            skLineSegment(sketch, "E454.top", {"start": v(-5.6, 30.48) * mm, "end": v(-2.42, 30.48) * mm});
            skLineSegment(sketch, "E454.left", {"start": v(-5.6, 34.26) * mm, "end": v(-5.6, 30.48) * mm});
            skLineSegment(sketch, "E454.right", {"start": v(-2.42, 34.26) * mm, "end": v(-2.42, 30.48) * mm});
            skLineSegment(sketch, "E455.bottom", {"start": v(-0.9, 34.32) * mm, "end": v(2.34, 34.32) * mm});
            skLineSegment(sketch, "E455.top", {"start": v(-0.9, 30.53) * mm, "end": v(2.34, 30.53) * mm});
            skLineSegment(sketch, "E455.left", {"start": v(-0.9, 34.32) * mm, "end": v(-0.9, 30.53) * mm});
            skLineSegment(sketch, "E455.right", {"start": v(2.34, 34.32) * mm, "end": v(2.34, 30.53) * mm});
            skLineSegment(sketch, "E456.bottom", {"start": v(-2.42, 30.48) * mm, "end": v(-3.99, 30.48) * mm});
            skLineSegment(sketch, "E456.top", {"start": v(-2.42, 32.37) * mm, "end": v(-3.99, 32.37) * mm});
            skLineSegment(sketch, "E456.left", {"start": v(-2.42, 30.48) * mm, "end": v(-2.42, 32.37) * mm});
            skLineSegment(sketch, "E456.right", {"start": v(-3.99, 30.48) * mm, "end": v(-3.99, 32.37) * mm});
            skLineSegment(sketch, "E457.bottom", {"start": v(-0.9, 30.53) * mm, "end": v(0.85, 30.53) * mm});
            skLineSegment(sketch, "E457.top", {"start": v(-0.9, 32.43) * mm, "end": v(0.85, 32.43) * mm});
            skLineSegment(sketch, "E457.left", {"start": v(-0.9, 30.53) * mm, "end": v(-0.9, 32.43) * mm});
            skLineSegment(sketch, "E457.right", {"start": v(0.85, 30.53) * mm, "end": v(0.85, 32.43) * mm});
            skLineSegment(sketch, "E458.bottom", {"start": v(-8.75, 28.61) * mm, "end": v(-13.59, 28.61) * mm});
            skLineSegment(sketch, "E458.top", {"start": v(-8.75, 32.32) * mm, "end": v(-10.31, 32.32) * mm});
            skLineSegment(sketch, "E458.left", {"start": v(-8.75, 28.61) * mm, "end": v(-8.75, 32.32) * mm});
            skLineSegment(sketch, "E458.right", {"start": v(-13.59, 28.61) * mm, "end": v(-13.59, 32.32) * mm});
            skLineSegment(sketch, "E459.bottom", {"start": v(-13.59, 32.32) * mm, "end": v(-10.31, 32.32) * mm});
            skLineSegment(sketch, "E459.top", {"start": v(-13.59, 34.25) * mm, "end": v(-11.84, 34.25) * mm});
            skLineSegment(sketch, "E459.left", {"start": v(-13.59, 32.32) * mm, "end": v(-13.59, 34.25) * mm});
            skLineSegment(sketch, "E459.right", {"start": v(-10.31, 32.32) * mm, "end": v(-10.31, 34.25) * mm});
            skLineSegment(sketch, "E460.bottom", {"start": v(-11.84, 36.17) * mm, "end": v(-10.14, 36.17) * mm});
            skLineSegment(sketch, "E460.top", {"start": v(-11.84, 34.25) * mm, "end": v(-8.75, 34.25) * mm});
            skLineSegment(sketch, "E460.right", {"start": v(-8.75, 36.17) * mm, "end": v(-8.75, 34.25) * mm});
            skLineSegment(sketch, "E461.bottom", {"start": v(-10.14, 37.85) * mm, "end": v(-7.18, 37.85) * mm});
            skLineSegment(sketch, "E461.top", {"start": v(-10.14, 36.17) * mm, "end": v(-7.18, 36.17) * mm});
            skLineSegment(sketch, "E461.right", {"start": v(-7.18, 37.85) * mm, "end": v(-7.18, 36.17) * mm});
            skLineSegment(sketch, "E462.bottom", {"start": v(-8.65, 39.77) * mm, "end": v(-7, 39.77) * mm});
            skLineSegment(sketch, "E462.right", {"start": v(5.6, 39.77) * mm, "end": v(5.6, 37.85) * mm});
            skLineSegment(sketch, "E463.bottom", {"start": v(-2.42, 34.26) * mm, "end": v(-0.9, 34.26) * mm});
            skLineSegment(sketch, "E463.left", {"start": v(-2.42, 34.26) * mm, "end": v(-2.42, 36.17) * mm});
            skLineSegment(sketch, "E463.right", {"start": v(-0.9, 34.26) * mm, "end": v(-0.9, 36.17) * mm});
            skLineSegment(sketch, "E464.top", {"start": v(-0.9, 36.17) * mm, "end": v(0.8, 36.17) * mm});
            skLineSegment(sketch, "E464.right", {"start": v(0.8, 37.85) * mm, "end": v(0.8, 36.17) * mm});
            skLineSegment(sketch, "E465.top", {"start": v(-2.42, 36.17) * mm, "end": v(-3.99, 36.17) * mm});
            skLineSegment(sketch, "E465.right", {"start": v(-3.99, 37.85) * mm, "end": v(-3.99, 36.17) * mm});
            skLineSegment(sketch, "E466.left", {"start": v(3.88, 37.85) * mm, "end": v(3.88, 36) * mm});
            skLineSegment(sketch, "E466.right", {"start": v(7.07, 37.85) * mm, "end": v(7.07, 36) * mm});
            skLineSegment(sketch, "E467.bottom", {"start": v(8.73, 36) * mm, "end": v(5.6, 36) * mm});
            skLineSegment(sketch, "E467.top", {"start": v(7.07, 34.25) * mm, "end": v(5.6, 34.25) * mm});
            skLineSegment(sketch, "E467.left", {"start": v(8.73, 36) * mm, "end": v(8.73, 34.25) * mm});
            skLineSegment(sketch, "E467.right", {"start": v(5.6, 36) * mm, "end": v(5.6, 34.25) * mm});
            skLineSegment(sketch, "E468.top", {"start": v(8.73, 28.62) * mm, "end": v(7.07, 28.62) * mm});
            skLineSegment(sketch, "E468.left", {"start": v(8.73, 34.15) * mm, "end": v(8.73, 28.62) * mm});
            skLineSegment(sketch, "E468.right", {"start": v(7.07, 34.15) * mm, "end": v(7.07, 32.39) * mm});
            skLineSegment(sketch, "E469.left", {"start": v(7.07, 34.15) * mm, "end": v(7.07, 34.25) * mm});
            skLineSegment(sketch, "E469.right", {"start": v(8.73, 34.15) * mm, "end": v(8.73, 34.25) * mm});
            skLineSegment(sketch, "E470.bottom", {"start": v(7.07, 28.62) * mm, "end": v(5.52, 28.62) * mm});
            skLineSegment(sketch, "E470.top", {"start": v(7.07, 32.39) * mm, "end": v(5.52, 32.39) * mm});
            skLineSegment(sketch, "E470.right", {"start": v(5.52, 28.62) * mm, "end": v(5.52, 32.39) * mm});
            skLineSegment(sketch, "E471.trimOffspring", {"start": v(0.8, 37.85) * mm, "end": v(3.88, 37.85) * mm});
            skPoint(sketch, "E472.orphan", {"position": v(-0.9, 37.85) * mm});
            skLineSegment(sketch, "E473.bottom", {"start": v(-4.02, 28.68) * mm, "end": v(0.8, 28.68) * mm});
            skLineSegment(sketch, "E473.top", {"start": v(-4.02, 26.69) * mm, "end": v(0.8, 26.69) * mm});
            skLineSegment(sketch, "E473.left", {"start": v(-4.02, 28.68) * mm, "end": v(-4.02, 26.69) * mm});
            skLineSegment(sketch, "E473.right", {"start": v(0.8, 28.68) * mm, "end": v(0.8, 26.69) * mm});
            skLineSegment(sketch, "E474.top", {"start": v(-11.9, 19.39) * mm, "end": v(-8.78, 19.39) * mm});
            skLineSegment(sketch, "E474.left", {"start": v(-11.9, 21.25) * mm, "end": v(-11.9, 19.39) * mm});
            skLineSegment(sketch, "E474.right", {"start": v(-8.78, 21.25) * mm, "end": v(-8.78, 19.39) * mm});
            skLineSegment(sketch, "E475.top", {"start": v(-7.14, 17.62) * mm, "end": v(-2.38, 17.62) * mm});
            skLineSegment(sketch, "E475.left", {"start": v(-7.14, 21.38) * mm, "end": v(-7.14, 17.62) * mm});
            skLineSegment(sketch, "E475.right", {"start": v(-2.38, 21.38) * mm, "end": v(-2.38, 17.62) * mm});
            skLineSegment(sketch, "E476.bottom", {"start": v(-0.77, 21.35) * mm, "end": v(0.9, 21.35) * mm});
            skLineSegment(sketch, "E476.top", {"start": v(-0.77, 17.62) * mm, "end": v(3.9, 17.62) * mm});
            skLineSegment(sketch, "E476.left", {"start": v(-0.77, 21.35) * mm, "end": v(-0.77, 17.62) * mm});
            skLineSegment(sketch, "E476.right", {"start": v(3.9, 21.35) * mm, "end": v(3.9, 17.62) * mm});
            skLineSegment(sketch, "E477.left", {"start": v(-5.56, 23.2) * mm, "end": v(-5.56, 21.26) * mm});
            skLineSegment(sketch, "E477.right", {"start": v(-4.03, 23.2) * mm, "end": v(-4.03, 21.26) * mm});
            skLineSegment(sketch, "E478.bottom", {"start": v(-7.15, 24.98) * mm, "end": v(-2.52, 24.98) * mm});
            skLineSegment(sketch, "E478.top", {"start": v(-7.15, 23.2) * mm, "end": v(-5.56, 23.2) * mm});
            skLineSegment(sketch, "E478.left", {"start": v(-7.15, 24.98) * mm, "end": v(-7.15, 23.2) * mm});
            skLineSegment(sketch, "E478.right", {"start": v(-2.52, 24.98) * mm, "end": v(-2.52, 23.2) * mm});
            skLineSegment(sketch, "E479.bottom", {"start": v(-0.8, 24.99) * mm, "end": v(3.9, 24.99) * mm});
            skLineSegment(sketch, "E479.top", {"start": v(-0.8, 23.22) * mm, "end": v(0.9, 23.22) * mm});
            skLineSegment(sketch, "E479.left", {"start": v(-0.8, 24.99) * mm, "end": v(-0.8, 23.22) * mm});
            skLineSegment(sketch, "E479.right", {"start": v(3.9, 24.99) * mm, "end": v(3.9, 23.22) * mm});
            skLineSegment(sketch, "E480.left", {"start": v(0.9, 23.22) * mm, "end": v(0.9, 21.35) * mm});
            skLineSegment(sketch, "E480.right", {"start": v(2.32, 23.22) * mm, "end": v(2.32, 21.35) * mm});
            skLineSegment(sketch, "E481.bottom", {"start": v(-11.8, 26.82) * mm, "end": v(-8.76, 26.82) * mm});
            skLineSegment(sketch, "E481.top", {"start": v(-10.34, 23.25) * mm, "end": v(-8.76, 23.25) * mm});
            skLineSegment(sketch, "E481.left", {"start": v(-11.8, 26.82) * mm, "end": v(-11.8, 24.95) * mm});
            skLineSegment(sketch, "E481.right", {"start": v(-8.76, 26.82) * mm, "end": v(-8.76, 23.25) * mm});
            skLineSegment(sketch, "E482.left", {"start": v(-11.8, 23.25) * mm, "end": v(-11.8, 21.25) * mm});
            skLineSegment(sketch, "E482.right", {"start": v(-10.34, 23.25) * mm, "end": v(-10.34, 21.25) * mm});
            skLineSegment(sketch, "E483.bottom", {"start": v(-11.8, 24.95) * mm, "end": v(-13.54, 24.95) * mm});
            skLineSegment(sketch, "E483.top", {"start": v(-11.8, 23.25) * mm, "end": v(-13.54, 23.25) * mm});
            skLineSegment(sketch, "E483.right", {"start": v(-13.54, 24.95) * mm, "end": v(-13.54, 23.25) * mm});
            skLineSegment(sketch, "E484.bottom", {"start": v(5.48, 26.85) * mm, "end": v(8.59, 26.85) * mm});
            skLineSegment(sketch, "E484.top", {"start": v(5.48, 23.15) * mm, "end": v(7.09, 23.15) * mm});
            skLineSegment(sketch, "E484.left", {"start": v(5.48, 26.85) * mm, "end": v(5.48, 23.15) * mm});
            skLineSegment(sketch, "E484.right", {"start": v(8.59, 26.85) * mm, "end": v(8.59, 25) * mm});
            skLineSegment(sketch, "E485.bottom", {"start": v(8.59, 25) * mm, "end": v(10.32, 25) * mm});
            skLineSegment(sketch, "E485.top", {"start": v(8.59, 23.15) * mm, "end": v(10.32, 23.15) * mm});
            skLineSegment(sketch, "E485.right", {"start": v(10.32, 25) * mm, "end": v(10.32, 23.15) * mm});
            skLineSegment(sketch, "E486.top", {"start": v(8.59, 19.44) * mm, "end": v(7.09, 19.44) * mm});
            skLineSegment(sketch, "E486.left", {"start": v(8.59, 23.15) * mm, "end": v(8.59, 19.44) * mm});
            skLineSegment(sketch, "E487.bottom", {"start": v(7.09, 21.3) * mm, "end": v(5.55, 21.3) * mm});
            skLineSegment(sketch, "E487.top", {"start": v(7.09, 19.43) * mm, "end": v(5.55, 19.43) * mm});
            skLineSegment(sketch, "E487.right", {"start": v(5.55, 21.3) * mm, "end": v(5.55, 19.43) * mm});
            skLineSegment(sketch, "E488.trimOffspring", {"start": v(-10.34, 21.25) * mm, "end": v(-8.78, 21.25) * mm});
            skLineSegment(sketch, "E489.trimOffspring", {"start": v(-4.03, 23.2) * mm, "end": v(-2.52, 23.2) * mm});
            skLineSegment(sketch, "E490.trimOffspring", {"start": v(-4.03, 21.38) * mm, "end": v(-2.38, 21.38) * mm});
            skLineSegment(sketch, "E491.trimOffspring", {"start": v(2.32, 23.22) * mm, "end": v(3.9, 23.22) * mm});
            skLineSegment(sketch, "E492.trimOffspring", {"start": v(2.32, 21.35) * mm, "end": v(3.9, 21.35) * mm});
            skLineSegment(sketch, "E493", {"start": v(-30.84, -10.04) * mm, "end": v(-26.16, -10.04) * mm});
            skLineSegment(sketch, "E494", {"start": v(-26.16, -10.04) * mm, "end": v(-26.16, -11.83) * mm});
            skLineSegment(sketch, "E495", {"start": v(-26.16, -11.83) * mm, "end": v(-19.84, -11.83) * mm});
            skLineSegment(sketch, "E496.bottom", {"start": v(-42.22, -8.58) * mm, "end": v(-43.76, -8.58) * mm});
            skLineSegment(sketch, "E496.top", {"start": v(-42.22, -5.66) * mm, "end": v(-43.76, -5.66) * mm});
            skLineSegment(sketch, "E496.left", {"start": v(-42.22, -8.58) * mm, "end": v(-42.22, -5.66) * mm});
            skLineSegment(sketch, "E496.right", {"start": v(-43.76, -8.58) * mm, "end": v(-43.76, -5.66) * mm});
            skLineSegment(sketch, "E497.bottom", {"start": v(-40.93, -14.87) * mm, "end": v(-42.3, -14.87) * mm});
            skLineSegment(sketch, "E497.top", {"start": v(-40.93, -16.21) * mm, "end": v(-42.3, -16.21) * mm});
            skLineSegment(sketch, "E497.left", {"start": v(-40.93, -14.87) * mm, "end": v(-40.93, -16.21) * mm});
            skLineSegment(sketch, "E497.right", {"start": v(-42.3, -14.87) * mm, "end": v(-42.3, -16.21) * mm});
            skLineSegment(sketch, "E498.bottom", {"start": v(-39.58, -16.35) * mm, "end": v(-40.93, -16.35) * mm});
            skLineSegment(sketch, "E498.top", {"start": v(-39.58, -17.87) * mm, "end": v(-40.93, -17.87) * mm});
            skLineSegment(sketch, "E498.right", {"start": v(-40.93, -16.35) * mm, "end": v(-40.93, -17.87) * mm});
            skLineSegment(sketch, "E499.top", {"start": v(-43.76, 3.35) * mm, "end": v(-42.35, 3.35) * mm});
            skLineSegment(sketch, "E499.left", {"start": v(-43.76, 4.94) * mm, "end": v(-43.76, 3.35) * mm});
            skLineSegment(sketch, "E499.right", {"start": v(-42.35, 4.94) * mm, "end": v(-42.35, 3.35) * mm});
            skLineSegment(sketch, "E500.bottom", {"start": v(-42.35, 3.35) * mm, "end": v(-40.93, 3.35) * mm});
            skLineSegment(sketch, "E500.top", {"start": v(-42.35, 1.92) * mm, "end": v(-40.93, 1.92) * mm});
            skLineSegment(sketch, "E500.left", {"start": v(-42.35, 3.35) * mm, "end": v(-42.35, 1.92) * mm});
            skLineSegment(sketch, "E500.right", {"start": v(-40.93, 3.35) * mm, "end": v(-40.93, 1.92) * mm});
            skLineSegment(sketch, "E501.bottom", {"start": v(-40.93, 3.35) * mm, "end": v(-40.93, 3.35) * mm});
            skLineSegment(sketch, "E501.top", {"start": v(-40.93, 3.21) * mm, "end": v(-40.93, 3.21) * mm});
            skLineSegment(sketch, "E501.left", {"start": v(-40.93, 3.35) * mm, "end": v(-40.93, 3.21) * mm});
            skLineSegment(sketch, "E501.right", {"start": v(-40.93, 3.35) * mm, "end": v(-40.93, 3.21) * mm});
            skLineSegment(sketch, "E502.bottom", {"start": v(-40.93, 3.35) * mm, "end": v(-39.48, 3.35) * mm});
            skLineSegment(sketch, "E502.top", {"start": v(-40.93, 4.94) * mm, "end": v(-39.48, 4.94) * mm});
            skLineSegment(sketch, "E502.left", {"start": v(-40.93, 3.35) * mm, "end": v(-40.93, 4.94) * mm});
            skLineSegment(sketch, "E502.right", {"start": v(-39.48, 3.35) * mm, "end": v(-39.48, 4.94) * mm});
            skLineSegment(sketch, "E503.bottom", {"start": v(-40.93, 4.94) * mm, "end": v(-42.35, 4.94) * mm});
            skLineSegment(sketch, "E503.top", {"start": v(-40.93, 6.3) * mm, "end": v(-42.35, 6.3) * mm});
            skLineSegment(sketch, "E503.left", {"start": v(-40.93, 4.94) * mm, "end": v(-40.93, 6.3) * mm});
            skLineSegment(sketch, "E504.bottom", {"start": v(-40.93, 7.86) * mm, "end": v(-36.63, 7.86) * mm});
            skLineSegment(sketch, "E504.top", {"start": v(-40.93, 6.43) * mm, "end": v(-36.63, 6.43) * mm});
            skLineSegment(sketch, "E504.left", {"start": v(-40.93, 7.86) * mm, "end": v(-40.93, 6.43) * mm});
            skLineSegment(sketch, "E504.right", {"start": v(-36.63, 7.86) * mm, "end": v(-36.63, 6.43) * mm});
            skLineSegment(sketch, "E505.bottom", {"start": v(-39.48, 4.94) * mm, "end": v(-38.07, 4.94) * mm});
            skLineSegment(sketch, "E505.top", {"start": v(-39.48, 6.43) * mm, "end": v(-38.07, 6.43) * mm});
            skLineSegment(sketch, "E505.left", {"start": v(-39.48, 4.94) * mm, "end": v(-39.48, 6.43) * mm});
            skLineSegment(sketch, "E505.right", {"start": v(-38.07, 4.94) * mm, "end": v(-38.07, 6.43) * mm});
            skLineSegment(sketch, "E506.bottom", {"start": v(-39.48, 3.35) * mm, "end": v(-38.02, 3.35) * mm});
            skLineSegment(sketch, "E506.top", {"start": v(-39.48, 1.92) * mm, "end": v(-38.02, 1.92) * mm});
            skLineSegment(sketch, "E506.left", {"start": v(-39.48, 3.35) * mm, "end": v(-39.48, 1.92) * mm});
            skLineSegment(sketch, "E506.right", {"start": v(-38.02, 3.35) * mm, "end": v(-38.02, 1.92) * mm});
            skLineSegment(sketch, "E507.bottom", {"start": v(-38.07, 4.94) * mm, "end": v(-36.59, 4.94) * mm});
            skLineSegment(sketch, "E507.top", {"start": v(-38.07, 3.59) * mm, "end": v(-36.59, 3.59) * mm});
            skLineSegment(sketch, "E507.left", {"start": v(-38.07, 4.94) * mm, "end": v(-38.07, 3.59) * mm});
            skLineSegment(sketch, "E507.right", {"start": v(-36.59, 4.94) * mm, "end": v(-36.59, 3.59) * mm});
            skLineSegment(sketch, "E508.bottom", {"start": v(-36.63, 6.43) * mm, "end": v(-35.2, 6.43) * mm});
            skLineSegment(sketch, "E508.top", {"start": v(-36.63, 4.83) * mm, "end": v(-35.2, 4.83) * mm});
            skLineSegment(sketch, "E508.left", {"start": v(-36.63, 6.43) * mm, "end": v(-36.63, 4.83) * mm});
            skLineSegment(sketch, "E508.right", {"start": v(-35.2, 6.43) * mm, "end": v(-35.2, 4.83) * mm});
            skLineSegment(sketch, "E509", {"start": v(-7.18, 37.85) * mm, "end": v(-3.99, 37.85) * mm});
            skLineSegment(sketch, "E510", {"start": v(3.88, 36) * mm, "end": v(5.6, 36) * mm});
            skPoint(sketch, "E511.middle", {"position": v(182.74, 291.47) * mm});
            skLineSegment(sketch, "E512.bottom", {"start": v(418.8, 99.47) * mm, "end": v(260.26, 99.47) * mm});
            skLineSegment(sketch, "E512.top", {"start": v(260.26, 483.47) * mm, "end": v(107.1, 483.47) * mm});
            skLineSegment(sketch, "E512.left", {"start": v(418.8, 99.47) * mm, "end": v(418.8, 155.71) * mm});
            skLineSegment(sketch, "E512.right", {"start": v(-53.32, 99.47) * mm, "end": v(-53.32, 155.71) * mm});
            skLineSegment(sketch, "E513.top", {"start": v(-53.32, 489.8) * mm, "end": v(107.1, 489.8) * mm});
            skLineSegment(sketch, "E513.left", {"start": v(-53.32, 483.47) * mm, "end": v(-53.32, 489.8) * mm});
            skLineSegment(sketch, "E513.right", {"start": v(107.1, 483.47) * mm, "end": v(107.1, 489.8) * mm});
            skLineSegment(sketch, "E514.MirrorCS", {"start": v(260.26, 483.47) * mm, "end": v(260.26, 489.8) * mm});
            skLineSegment(sketch, "E515.MirrorCS", {"start": v(420.68, 487.92) * mm, "end": v(260.26, 487.92) * mm});
            skLineSegment(sketch, "E516.MirrorCS", {"start": v(420.68, 483.47) * mm, "end": v(420.68, 487.92) * mm});
            skLineSegment(sketch, "E517.top", {"start": v(107.1, 93.14) * mm, "end": v(260.26, 93.14) * mm});
            skLineSegment(sketch, "E517.left", {"start": v(107.1, 99.47) * mm, "end": v(107.1, 93.14) * mm});
            skLineSegment(sketch, "E517.right", {"start": v(260.26, 99.47) * mm, "end": v(260.26, 93.14) * mm});
            skLineSegment(sketch, "E518.trimOffspring", {"start": v(107.1, 99.47) * mm, "end": v(-53.32, 99.47) * mm});
            skLineSegment(sketch, "E519.bottom", {"start": v(425.13, 155.71) * mm, "end": v(418.8, 155.71) * mm});
            skLineSegment(sketch, "E519.top", {"start": v(425.13, 427.22) * mm, "end": v(418.8, 427.22) * mm});
            skLineSegment(sketch, "E519.left", {"start": v(425.13, 155.71) * mm, "end": v(425.13, 427.22) * mm});
            skLineSegment(sketch, "E519.right", {"start": v(-59.65, 155.71) * mm, "end": v(-59.65, 427.22) * mm});
            skLineSegment(sketch, "E520.trimOffspring", {"start": v(-53.32, 427.22) * mm, "end": v(-59.65, 427.22) * mm});
            skLineSegment(sketch, "E521.trimOffspring", {"start": v(-53.32, 155.71) * mm, "end": v(-59.65, 155.71) * mm});
            skLineSegment(sketch, "E522.trimOffspring", {"start": v(-53.32, 427.22) * mm, "end": v(-53.32, 483.47) * mm});
            skLineSegment(sketch, "E523.trimOffspring", {"start": v(418.8, 427.22) * mm, "end": v(418.8, 483.47) * mm});
            skLineSegment(sketch, "E524", {"start": v(222.1, 417.6) * mm, "end": v(220, 417.6) * mm});
            skLineSegment(sketch, "E525", {"start": v(220, 417.6) * mm, "end": v(220, 415.5) * mm});
            skLineSegment(sketch, "E526", {"start": v(220, 417.6) * mm, "end": v(217.9, 417.6) * mm});
            skLineSegment(sketch, "E527", {"start": v(220, 318) * mm, "end": v(217.9, 318) * mm});
            skLineSegment(sketch, "E528", {"start": v(120.18, 415.5) * mm, "end": v(120.18, 417.6) * mm});
            skCircle(sketch, "E529", {"center": v(120.18, 417.6) * mm, "radius": 2.1 * mm});
            skCircle(sketch, "E530", {"center": v(120.18, 318) * mm, "radius": 2.1 * mm});
            skCircle(sketch, "E531", {"center": v(220, 318) * mm, "radius": 2.1 * mm});
            skCircle(sketch, "E532", {"center": v(220, 417.6) * mm, "radius": 2.1 * mm});
            skLineSegment(sketch, "E533.trimOffspring", {"start": v(220, 320.1) * mm, "end": v(220, 318) * mm});
            skLineSegment(sketch, "E534.trimOffspring", {"start": v(122.28, 417.6) * mm, "end": v(120.18, 417.6) * mm});
            skLineSegment(sketch, "E535.bottom", {"start": v(57.39, 183.9) * mm, "end": v(22.39, 183.9) * mm});
            skLineSegment(sketch, "E535.top", {"start": v(57.39, 452.13) * mm, "end": v(22.39, 452.13) * mm});
            skLineSegment(sketch, "E535.right", {"start": v(22.39, 183.9) * mm, "end": v(22.39, 452.13) * mm});
            skPoint(sketch, "E535.middle", {"position": v(20.1, 318) * mm});
            skPoint(sketch, "E536.orphan", {"position": v(22.39, 318) * mm});
            skLineSegment(sketch, "E537.bottom", {"start": v(-50.54, -502.77) * mm, "end": v(104.63, -502.77) * mm});
            skLineSegment(sketch, "E537.top", {"start": v(-210.95, -543.27) * mm, "end": v(-50.54, -543.27) * mm});
            skLineSegment(sketch, "E537.left", {"start": v(-210.95, -502.77) * mm, "end": v(-210.95, -543.27) * mm});
            skLineSegment(sketch, "E537.right", {"start": v(265.05, -502.77) * mm, "end": v(265.05, -543.27) * mm});
            skLineSegment(sketch, "E538.top", {"start": v(104.63, -502.77) * mm, "end": v(-50.54, -502.77) * mm});
            skLineSegment(sketch, "E539.left", {"start": v(-210.95, -502.77) * mm, "end": v(-210.95, -498.32) * mm});
            skLineSegment(sketch, "E540.MirrorCS", {"start": v(265.05, -502.77) * mm, "end": v(265.05, -498.32) * mm});
            skLineSegment(sketch, "E541.top", {"start": v(-50.54, -547.72) * mm, "end": v(104.63, -547.72) * mm});
            skLineSegment(sketch, "E541.left", {"start": v(-50.54, -543.27) * mm, "end": v(-50.54, -547.72) * mm});
            skLineSegment(sketch, "E541.right", {"start": v(104.63, -543.27) * mm, "end": v(104.63, -547.72) * mm});
            skLineSegment(sketch, "E542.trimOffspring", {"start": v(104.63, -543.27) * mm, "end": v(265.05, -543.27) * mm});
            skLineSegment(sketch, "E543", {"start": v(-50.54, -502.77) * mm, "end": v(-50.54, -512.03) * mm});
            skLineSegment(sketch, "E544", {"start": v(104.63, -512.03) * mm, "end": v(104.63, -502.77) * mm});
            skLineSegment(sketch, "E545", {"start": v(104.63, -512.03) * mm, "end": v(265.05, -512.03) * mm});
            skLineSegment(sketch, "E546", {"start": v(-50.54, -512.03) * mm, "end": v(-210.95, -512.03) * mm});
            skArc(sketch, "E547", {"start": v(57.39, 183.9) * mm, "mid": v(111.27, 318) * mm, "end": v(57.39, 452.13) * mm});
            skLineSegment(sketch, "E548", {"start": v(418.8, 483.47) * mm, "end": v(418.8, 487.92) * mm});
            skLineSegment(sketch, "E549", {"start": v(260.26, 60.52) * mm, "end": v(420.68, 60.52) * mm});
            skPoint(sketch, "E550.MirrorCS.start.orphan", {"position": v(420.68, 58.64) * mm});
            skLineSegment(sketch, "E551", {"start": v(418.8, 54.19) * mm, "end": v(418.8, 60.52) * mm});
            skSolve(sketch);
        }
        {
            var Q0;
            Q0=makeQuery(id+"F0.imprint","IMPRINT",FACE,{"disambiguationData":[TD([[makeQuery(id+"F0.imprint","IMPRINT",EDGE,{"derivedFrom":sQuery(id+"F0.wireOp",EDGE,"E512.bottom")}),-1.0]])]});
            var Q1;
            Q1=makeQuery(id+"F0.imprint","IMPRINT",FACE,{"disambiguationData":[TD([[makeQuery(id+"F0.imprint","IMPRINT",EDGE,{"derivedFrom":sQuery(id+"F0.wireOp",EDGE,"E0.bottom")}),1.0]])]});
            var Q2;
            Q2=makeQuery(id+"F0.imprint","IMPRINT",FACE,{"disambiguationData":[TD([[makeQuery(id+"F0.imprint","IMPRINT",EDGE,{"derivedFrom":sQuery(id+"F0.wireOp",EDGE,"E537.top")}),1.0]])]});
            extrude(context, id + "F1", {"entities" : qUnion([Q0, Q1, Q2]), "depth" : 4.45 * mm, "offsetDistance" : 25 * mm});
        }
    });
